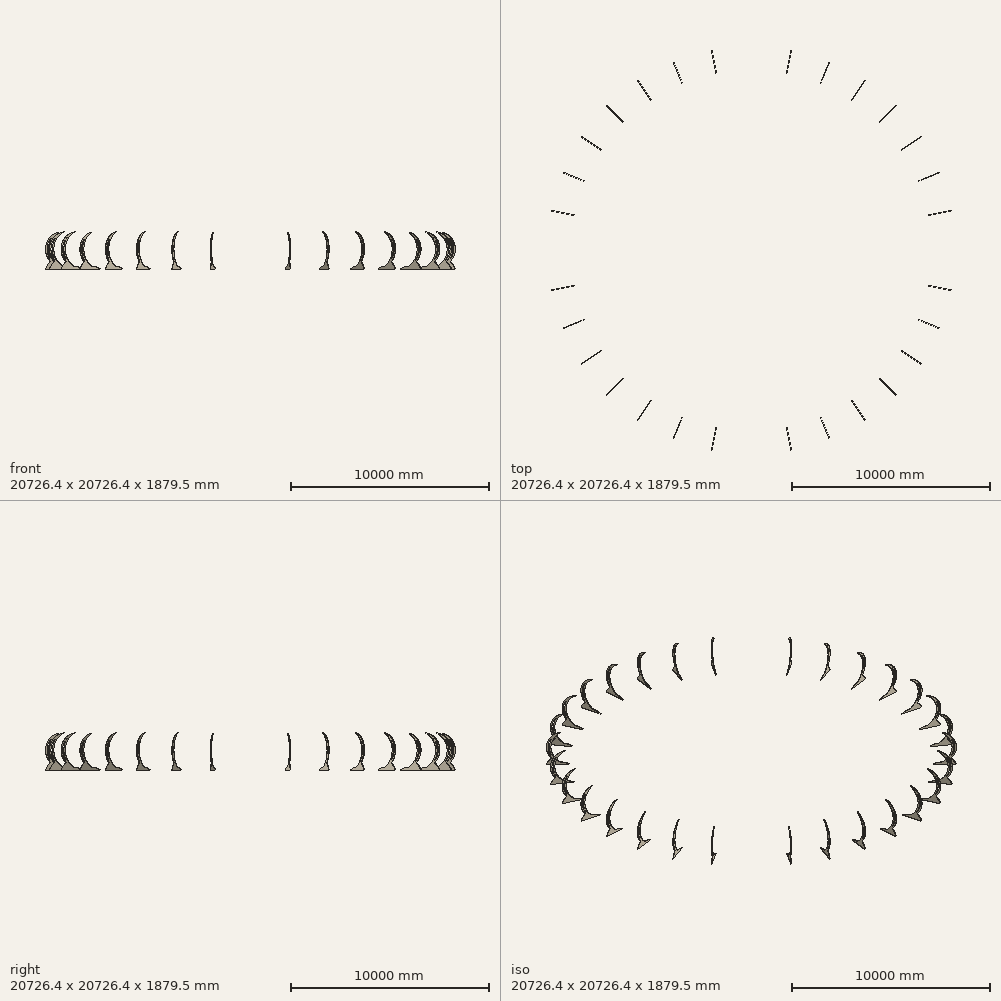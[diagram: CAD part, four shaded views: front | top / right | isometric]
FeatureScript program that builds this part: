
annotation { "Feature Type Name" : "Feature", "Feature Type Description" : "" }
export const myFeature = defineFeature(function(context is Context, id is Id, definition is map)
    precondition{}
    {
        {
            var Q0;
            Q0=qCreatedBy(makeId("Front.planeOp"),FACE);
            var sketch = newSketch(context, id + "F0", { "sketchPlane" : qUnion([Q0])});
            skLineSegment(sketch, "E0.1", {"start": v(-10363.2, 0) * mm, "end": v(-10363.2, 1219.2) * mm, "construction": true});
            skLineSegment(sketch, "E0.7", {"start": v(-9144, 0) * mm, "end": v(-10363.2, 0) * mm, "construction": true});
            skArc(sketch, "E0.8", {"start": v(-9241.93, -3.92) * mm, "mid": v(-9367.59, 73.04) * mm, "end": v(-9502.79, 131.63) * mm, "construction": true});
            skLineSegment(sketch, "E0.10", {"start": v(-9144, 0) * mm, "end": v(-9144, 1219.2) * mm, "construction": true});
            skLineSegment(sketch, "E1.top", {"start": v(-10363.2, 2438.4) * mm, "end": v(-9144, 2438.4) * mm, "construction": true});
            skLineSegment(sketch, "E1.left", {"start": v(-10363.2, 1219.2) * mm, "end": v(-10363.2, 2438.4) * mm, "construction": true});
            skLineSegment(sketch, "E1.right", {"start": v(-9144, 1219.2) * mm, "end": v(-9144, 2438.4) * mm, "construction": true});
            skLineSegment(sketch, "E2", {"start": v(-10363.2, 1219.2) * mm, "end": v(-9144, 1219.2) * mm, "construction": true});
            skLineSegment(sketch, "E3", {"start": v(-9753.6, 2438.4) * mm, "end": v(-9753.6, 0) * mm, "construction": true});
            skArc(sketch, "E4", {"start": v(-10093.04, 361.13) * mm, "mid": v(-10247.75, 195.25) * mm, "end": v(-10363.2, 0) * mm});
            skLineSegment(sketch, "E5", {"start": v(-9408.3, 60.26) * mm, "end": v(-9595.1, 1879.5) * mm, "construction": true});
            skArc(sketch, "E6", {"start": v(-9595.1, 1879.5) * mm, "mid": v(-10318.96, 1276.05) * mm, "end": v(-10093.04, 361.13) * mm});
            skArc(sketch, "E7", {"start": v(-9595.1, 1879.5) * mm, "mid": v(-10136.83, 1039.6) * mm, "end": v(-9674.58, 153.48) * mm});
            skLineSegment(sketch, "E8", {"start": v(-10363.2, 0) * mm, "end": v(-9144, 0) * mm});
            skArc(sketch, "E9.0", {"start": v(-10033.51, 1588.72) * mm, "mid": v(-10286.9, 1012.18) * mm, "end": v(-10052.1, 427.81) * mm});
            skArc(sketch, "E9.1", {"start": v(-10033.51, 1588.72) * mm, "mid": v(-10213.94, 1011) * mm, "end": v(-10052.1, 427.81) * mm});
            skPoint(sketch, "E10.center", {"position": v(-9753.6, 1219.2) * mm});
            skArc(sketch, "E11", {"start": v(-9144, 0) * mm, "mid": v(-9400.61, 106.73) * mm, "end": v(-9674.58, 153.48) * mm});
            skPoint(sketch, "E0.9.start.orphan", {"position": v(-9404.85, 135.55) * mm});
            skArc(sketch, "E12.1.0", {"start": v(-9414.16, 2077.27) * mm, "mid": v(-9259.45, 2243.15) * mm, "end": v(-9144, 2438.4) * mm, "construction": true});
            skArc(sketch, "E12.1.1", {"start": v(-9912.1, 558.9) * mm, "mid": v(-9188.24, 1162.35) * mm, "end": v(-9414.16, 2077.27) * mm, "construction": true});
            skArc(sketch, "E12.1.2", {"start": v(-9473.69, 849.68) * mm, "mid": v(-9220.3, 1426.22) * mm, "end": v(-9455.1, 2010.59) * mm, "construction": true});
            skArc(sketch, "E12.1.3", {"start": v(-9473.69, 849.68) * mm, "mid": v(-9293.26, 1427.4) * mm, "end": v(-9455.1, 2010.59) * mm, "construction": true});
            skArc(sketch, "E12.1.4", {"start": v(-9912.1, 558.9) * mm, "mid": v(-9370.37, 1398.8) * mm, "end": v(-9832.62, 2284.92) * mm, "construction": true});
            skArc(sketch, "E12.1.5", {"start": v(-10363.2, 2438.4) * mm, "mid": v(-10106.59, 2331.67) * mm, "end": v(-9832.62, 2284.92) * mm, "construction": true});
            skSolve(sketch);
        }
        {
            var Q0;
            Q0 = qSketchRegion(id + "F0", true);
            extrude(context, id + "F1", {"entities" : qUnion([Q0]), "depth" : 12.7 * mm, "hasSecondDirection" : true, "secondDirectionOppositeDirection" : true, "secondDirectionDepth" : 12.7 * mm});
        }
        {
            var Q0;
            Q0=qCreatedBy(makeId("Front.planeOp"),FACE);
            var sketch = newSketch(context, id + "F2", { "sketchPlane" : qUnion([Q0])});
            skLineSegment(sketch, "E13.bottom", {"start": v(-9144, 0) * mm, "end": v(-10363.2, 0) * mm});
            skLineSegment(sketch, "E13.top", {"start": v(-9144, 1219.2) * mm, "end": v(-10363.2, 1219.2) * mm, "construction": true});
            skLineSegment(sketch, "E13.left", {"start": v(-9144, 0) * mm, "end": v(-9144, 1219.2) * mm, "construction": true});
            skLineSegment(sketch, "E13.right", {"start": v(-10363.2, 0) * mm, "end": v(-10363.2, 1219.2) * mm, "construction": true});
            skArc(sketch, "E14", {"start": v(-9144, 0) * mm, "mid": v(-9269.66, 76.95) * mm, "end": v(-9404.85, 135.55) * mm});
            skLineSegment(sketch, "E15", {"start": v(0, 1828.8) * mm, "end": v(0, 4267.2) * mm, "construction": true});
            skLineSegment(sketch, "E16", {"start": v(-5181.6, 12008.6) * mm, "end": v(-5181.6, -5912.6) * mm, "construction": true});
            skEllipse(sketch, "E17", {"center": v(-5181.6, 3048) * mm, "majorRadius": 8960.6 * mm, "minorRadius": 5181.6 * mm, "majorAxis": v(0, 1), "construction": true});
            skPoint(sketch, "E18", {"position": v(-10363.2, 3048) * mm});
            skPoint(sketch, "E19", {"position": v(0, 3048) * mm});
            skEllipticalArc(sketch, "E20", {});
            skPoint(sketch, "E21", {"position": v(-10363.2, 663.58) * mm});
            skPoint(sketch, "E22", {"position": v(-9632.3, 1219.2) * mm});
            skArc(sketch, "E23.trimOffspring", {"start": v(-9972.96, 172) * mm, "mid": v(-10176.9, 106.03) * mm, "end": v(-10363.2, 0) * mm});
            skEllipticalArc(sketch, "E24.trimOffspring", {});
            skEllipticalArc(sketch, "E25", {});
            skFitSpline(sketch, "E26.0", {"points": [v(-10286.97, 669.24) * mm, v(-10287.02, 663.58) * mm, v(-10286.97, 657.92) * mm, v(-10286.79, 650.39) * mm, v(-10286.32, 640.99) * mm, v(-10285.4, 629.74) * mm, v(-10283.7, 614.8) * mm, v(-10280.66, 596.2) * mm, v(-10275.57, 574.03) * mm, v(-10269.05, 552.04) * mm, v(-10258.44, 522.98) * mm, v(-10241.6, 487.22) * mm, v(-10220, 452.43) * mm, v(-10199.87, 425.37) * mm, v(-10183.35, 405.5) * mm, v(-10165.42, 386.1) * mm, v(-10149.3, 370.36) * mm, v(-10135.72, 358.07) * mm, v(-10125.18, 349) * mm, v(-10116.1, 341.57) * mm, v(-10108.68, 335.7) * mm, v(-10103.02, 331.35) * mm, v(-10097.29, 327.05) * mm, v(-10089.55, 321.38) * mm, v(-10079.7, 314.43) * mm, v(-10067.62, 306.32) * mm, v(-10051.15, 295.8) * mm, v(-10029.94, 283.24) * mm, v(-10003.5, 269.12) * mm, v(-9976.16, 255.98) * mm, v(-9938.56, 239.81) * mm, v(-9889.56, 222.2) * mm, v(-9838.32, 208.25) * mm, v(-9796.23, 199.37) * mm, v(-9764.18, 193.87) * mm, v(-9731.7, 189.56) * mm, v(-9704.32, 186.98) * mm, v(-9682.28, 185.52) * mm, v(-9665.68, 184.74) * mm, v(-9651.8, 184.35) * mm, v(-9640.66, 184.19) * mm, v(-9632.3, 184.15) * mm, v(-9623.93, 184.19) * mm, v(-9612.8, 184.35) * mm, v(-9598.92, 184.74) * mm, v(-9582.31, 185.52) * mm, v(-9560.27, 186.98) * mm, v(-9532.9, 189.56) * mm, v(-9500.42, 193.87) * mm, v(-9468.36, 199.37) * mm, v(-9426.27, 208.25) * mm, v(-9375.03, 222.2) * mm, v(-9326.04, 239.81) * mm, v(-9288.44, 255.98) * mm, v(-9261.1, 269.12) * mm, v(-9234.66, 283.24) * mm, v(-9213.44, 295.8) * mm, v(-9196.98, 306.32) * mm, v(-9184.9, 314.43) * mm, v(-9175.05, 321.38) * mm, v(-9167.3, 327.05) * mm, v(-9161.57, 331.35) * mm, v(-9155.91, 335.7) * mm, v(-9148.49, 341.57) * mm, v(-9139.42, 349) * mm, v(-9128.88, 358.07) * mm, v(-9115.3, 370.36) * mm, v(-9099.18, 386.1) * mm, v(-9081.24, 405.5) * mm, v(-9064.73, 425.37) * mm, v(-9044.6, 452.43) * mm, v(-9022.99, 487.22) * mm, v(-9006.15, 522.98) * mm, v(-8995.55, 552.04) * mm, v(-8989.02, 574.03) * mm, v(-8983.94, 596.2) * mm, v(-8980.9, 614.8) * mm, v(-8979.19, 629.74) * mm, v(-8978.27, 640.99) * mm, v(-8977.8, 650.39) * mm, v(-8977.62, 657.92) * mm, v(-8977.58, 663.58) * mm, v(-8977.62, 669.24) * mm, v(-8977.8, 676.77) * mm, v(-8978.27, 686.17) * mm, v(-8979.19, 697.42) * mm, v(-8980.9, 712.37) * mm, v(-8983.94, 730.97) * mm, v(-8989.02, 753.13) * mm, v(-8995.55, 775.12) * mm, v(-9006.15, 804.18) * mm, v(-9022.99, 839.94) * mm, v(-9044.6, 874.73) * mm, v(-9064.73, 901.8) * mm, v(-9081.24, 921.67) * mm, v(-9099.18, 941.07) * mm, v(-9115.3, 956.8) * mm, v(-9128.88, 969.1) * mm, v(-9139.42, 978.16) * mm, v(-9148.49, 985.6) * mm, v(-9155.91, 991.45) * mm, v(-9161.57, 995.8) * mm, v(-9167.3, 1000.11) * mm, v(-9175.05, 1005.78) * mm, v(-9184.9, 1012.73) * mm, v(-9196.98, 1020.84) * mm, v(-9213.44, 1031.36) * mm, v(-9234.66, 1043.92) * mm, v(-9261.1, 1058.04) * mm, v(-9288.44, 1071.18) * mm, v(-9326.04, 1087.35) * mm, v(-9375.03, 1104.95) * mm, v(-9426.27, 1118.9) * mm, v(-9468.36, 1127.79) * mm, v(-9500.42, 1133.29) * mm, v(-9532.9, 1137.6) * mm, v(-9560.27, 1140.18) * mm, v(-9582.31, 1141.64) * mm, v(-9598.92, 1142.42) * mm, v(-9612.8, 1142.81) * mm, v(-9623.93, 1142.97) * mm, v(-9632.3, 1143.01) * mm, v(-9640.66, 1142.97) * mm, v(-9651.8, 1142.81) * mm, v(-9665.68, 1142.42) * mm, v(-9682.28, 1141.64) * mm, v(-9704.32, 1140.18) * mm, v(-9731.7, 1137.6) * mm, v(-9764.18, 1133.29) * mm, v(-9796.23, 1127.79) * mm, v(-9838.32, 1118.9) * mm, v(-9889.56, 1104.95) * mm, v(-9938.56, 1087.35) * mm, v(-9976.16, 1071.18) * mm, v(-10003.5, 1058.04) * mm, v(-10029.94, 1043.92) * mm, v(-10051.15, 1031.36) * mm, v(-10067.62, 1020.84) * mm, v(-10079.7, 1012.73) * mm, v(-10089.55, 1005.78) * mm, v(-10097.29, 1000.11) * mm, v(-10103.02, 995.8) * mm, v(-10108.68, 991.45) * mm, v(-10116.1, 985.6) * mm, v(-10125.18, 978.16) * mm, v(-10135.72, 969.1) * mm, v(-10149.3, 956.8) * mm, v(-10165.42, 941.07) * mm, v(-10183.35, 921.67) * mm, v(-10199.87, 901.8) * mm, v(-10220, 874.73) * mm, v(-10241.6, 839.94) * mm, v(-10258.44, 804.18) * mm, v(-10269.05, 775.12) * mm, v(-10275.57, 753.13) * mm, v(-10280.66, 730.97) * mm, v(-10283.7, 712.37) * mm, v(-10285.4, 697.42) * mm, v(-10286.32, 686.17) * mm, v(-10286.79, 676.77) * mm, v(-10286.97, 669.24) * mm, v(-10287.02, 663.58) * mm, v(-10286.97, 657.92) * mm]});
            skFitSpline(sketch, "E27.trimOffspring", {"points": [v(-8791.4, 656.31) * mm, v(-8791.35, 663.58) * mm, v(-8791.4, 670.85) * mm, v(-8791.63, 680.52) * mm, v(-8792.18, 692.59) * mm, v(-8793.28, 707.01) * mm, v(-8795.31, 726.17) * mm, v(-8798.93, 749.93) * mm, v(-8804.96, 778.12) * mm, v(-8812.64, 805.9) * mm, v(-8825.03, 842.33) * mm, v(-8844.45, 886.58) * mm, v(-8868.9, 928.78) * mm, v(-8891.3, 961.13) * mm, v(-8909.5, 984.64) * mm, v(-8929.06, 1007.35) * mm, v(-8946.46, 1025.6) * mm, v(-8961.03, 1039.74) * mm, v(-8972.27, 1050.14) * mm, v(-8981.9, 1058.6) * mm, v(-8989.76, 1065.27) * mm, v(-8995.74, 1070.2) * mm, v(-9001.78, 1075.08) * mm, v(-9009.92, 1081.48) * mm, v(-9020.24, 1089.3) * mm, v(-9032.86, 1098.4) * mm, v(-9049.98, 1110.14) * mm, v(-9071.93, 1124.1) * mm, v(-9099.09, 1139.68) * mm, v(-9127, 1154.08) * mm, v(-9165.16, 1171.7) * mm, v(-9214.5, 1190.72) * mm, v(-9265.7, 1205.69) * mm, v(-9307.56, 1215.17) * mm, v(-9339.36, 1221.03) * mm, v(-9371.52, 1225.6) * mm, v(-9398.59, 1228.36) * mm, v(-9420.37, 1229.9) * mm, v(-9436.76, 1230.73) * mm, v(-9450.47, 1231.15) * mm, v(-9461.46, 1231.31) * mm, v(-9469.71, 1231.36) * mm, v(-9477.97, 1231.31) * mm, v(-9488.95, 1231.15) * mm, v(-9502.66, 1230.73) * mm, v(-9519.06, 1229.9) * mm, v(-9540.84, 1228.36) * mm, v(-9567.9, 1225.6) * mm, v(-9600.06, 1221.03) * mm, v(-9631.87, 1215.17) * mm, v(-9673.73, 1205.69) * mm, v(-9724.92, 1190.72) * mm, v(-9774.26, 1171.7) * mm, v(-9812.42, 1154.08) * mm, v(-9840.34, 1139.68) * mm, v(-9867.5, 1124.1) * mm, v(-9889.44, 1110.14) * mm, v(-9906.57, 1098.4) * mm, v(-9919.19, 1089.3) * mm, v(-9929.5, 1081.48) * mm, v(-9937.64, 1075.08) * mm, v(-9943.69, 1070.2) * mm, v(-9949.66, 1065.27) * mm, v(-9957.52, 1058.6) * mm, v(-9967.15, 1050.14) * mm, v(-9978.4, 1039.74) * mm, v(-9992.96, 1025.6) * mm, v(-10010.37, 1007.35) * mm, v(-10029.92, 984.64) * mm, v(-10048.12, 961.13) * mm, v(-10070.53, 928.78) * mm, v(-10094.97, 886.58) * mm, v(-10114.4, 842.33) * mm, v(-10126.79, 805.9) * mm, v(-10134.46, 778.12) * mm, v(-10140.49, 749.93) * mm, v(-10144.1, 726.17) * mm, v(-10146.15, 707.01) * mm, v(-10147.24, 692.59) * mm, v(-10147.8, 680.52) * mm, v(-10148.01, 670.85) * mm, v(-10148.07, 663.58) * mm, v(-10148.01, 656.31) * mm, v(-10147.8, 646.64) * mm, v(-10147.24, 634.58) * mm, v(-10146.15, 620.15) * mm, v(-10144.1, 601) * mm, v(-10140.49, 577.23) * mm, v(-10134.46, 549.05) * mm, v(-10126.79, 521.26) * mm, v(-10114.4, 484.83) * mm, v(-10094.97, 440.58) * mm, v(-10070.53, 398.38) * mm, v(-10048.12, 366.04) * mm, v(-10029.92, 342.53) * mm, v(-10010.37, 319.81) * mm, v(-9992.96, 301.57) * mm, v(-9978.4, 287.42) * mm, v(-9967.15, 277.03) * mm, v(-9957.52, 268.56) * mm, v(-9949.66, 261.9) * mm, v(-9943.69, 256.96) * mm, v(-9937.64, 252.08) * mm, v(-9929.5, 245.69) * mm, v(-9919.19, 237.86) * mm, v(-9906.57, 228.77) * mm, v(-9889.44, 217.02) * mm, v(-9867.5, 203.07) * mm, v(-9840.34, 187.49) * mm, v(-9812.42, 173.09) * mm, v(-9774.26, 155.47) * mm, v(-9724.92, 136.44) * mm, v(-9673.73, 121.48) * mm, v(-9631.87, 112) * mm, v(-9600.06, 106.14) * mm, v(-9567.9, 101.55) * mm, v(-9540.84, 98.8) * mm, v(-9519.06, 97.26) * mm, v(-9502.66, 96.43) * mm, v(-9488.95, 96.02) * mm, v(-9477.97, 95.85) * mm, v(-9469.71, 95.8) * mm, v(-9461.46, 95.85) * mm, v(-9450.47, 96.02) * mm, v(-9436.76, 96.43) * mm, v(-9420.37, 97.26) * mm, v(-9398.59, 98.8) * mm, v(-9371.52, 101.55) * mm, v(-9339.36, 106.14) * mm, v(-9307.56, 112) * mm, v(-9265.7, 121.48) * mm, v(-9214.5, 136.44) * mm, v(-9165.16, 155.47) * mm, v(-9127, 173.09) * mm, v(-9099.09, 187.49) * mm, v(-9071.93, 203.07) * mm, v(-9049.98, 217.02) * mm, v(-9032.86, 228.77) * mm, v(-9020.24, 237.86) * mm, v(-9009.92, 245.69) * mm, v(-9001.78, 252.08) * mm, v(-8995.74, 256.96) * mm, v(-8989.76, 261.9) * mm, v(-8981.9, 268.56) * mm, v(-8972.27, 277.03) * mm, v(-8961.03, 287.42) * mm, v(-8946.46, 301.57) * mm, v(-8929.06, 319.81) * mm, v(-8909.5, 342.53) * mm, v(-8891.3, 366.04) * mm, v(-8868.9, 398.38) * mm, v(-8844.45, 440.58) * mm, v(-8825.03, 484.83) * mm, v(-8812.64, 521.26) * mm, v(-8804.96, 549.05) * mm, v(-8798.93, 577.23) * mm, v(-8795.31, 601) * mm, v(-8793.28, 620.15) * mm, v(-8792.18, 634.58) * mm, v(-8791.63, 646.64) * mm, v(-8791.4, 656.31) * mm, v(-8791.35, 663.58) * mm, v(-8791.4, 670.85) * mm]});
            skFitSpline(sketch, "E28.trimOffspring", {"points": [v(-8791.41, 656.31) * mm, v(-8791.36, 663.58) * mm, v(-8791.41, 670.85) * mm, v(-8791.63, 680.52) * mm, v(-8792.18, 692.59) * mm, v(-8793.28, 707.01) * mm, v(-8795.32, 726.16) * mm, v(-8798.94, 749.93) * mm, v(-8804.96, 778.12) * mm, v(-8812.64, 805.9) * mm, v(-8825.03, 842.33) * mm, v(-8844.46, 886.58) * mm, v(-8868.9, 928.78) * mm, v(-8891.3, 961.13) * mm, v(-8909.5, 984.63) * mm, v(-8929.06, 1007.35) * mm, v(-8946.46, 1025.59) * mm, v(-8961.03, 1039.74) * mm, v(-8972.27, 1050.13) * mm, v(-8981.9, 1058.6) * mm, v(-8989.76, 1065.27) * mm, v(-8995.74, 1070.2) * mm, v(-9001.78, 1075.08) * mm, v(-9009.92, 1081.48) * mm, v(-9020.24, 1089.3) * mm, v(-9032.86, 1098.4) * mm, v(-9049.98, 1110.14) * mm, v(-9071.93, 1124.1) * mm, v(-9099.09, 1139.67) * mm, v(-9127, 1154.07) * mm, v(-9165.16, 1171.69) * mm, v(-9214.5, 1190.72) * mm, v(-9265.7, 1205.68) * mm, v(-9307.56, 1215.17) * mm, v(-9339.36, 1221.02) * mm, v(-9371.52, 1225.6) * mm, v(-9398.59, 1228.35) * mm, v(-9420.37, 1229.9) * mm, v(-9436.76, 1230.73) * mm, v(-9450.47, 1231.14) * mm, v(-9461.46, 1231.31) * mm, v(-9469.71, 1231.35) * mm, v(-9477.97, 1231.31) * mm, v(-9488.96, 1231.14) * mm, v(-9502.66, 1230.73) * mm, v(-9519.06, 1229.9) * mm, v(-9540.84, 1228.35) * mm, v(-9567.9, 1225.6) * mm, v(-9600.06, 1221.02) * mm, v(-9631.87, 1215.17) * mm, v(-9673.73, 1205.68) * mm, v(-9724.92, 1190.72) * mm, v(-9774.26, 1171.69) * mm, v(-9812.42, 1154.07) * mm, v(-9840.34, 1139.67) * mm, v(-9867.5, 1124.1) * mm, v(-9889.44, 1110.14) * mm, v(-9906.57, 1098.4) * mm, v(-9919.19, 1089.3) * mm, v(-9929.5, 1081.48) * mm, v(-9937.64, 1075.08) * mm, v(-9943.69, 1070.2) * mm, v(-9949.66, 1065.27) * mm, v(-9957.52, 1058.6) * mm, v(-9967.15, 1050.13) * mm, v(-9978.4, 1039.74) * mm, v(-9992.96, 1025.59) * mm, v(-10010.37, 1007.35) * mm, v(-10029.92, 984.63) * mm, v(-10048.12, 961.13) * mm, v(-10070.53, 928.78) * mm, v(-10094.97, 886.58) * mm, v(-10114.4, 842.33) * mm, v(-10126.78, 805.9) * mm, v(-10134.46, 778.12) * mm, v(-10140.49, 749.93) * mm, v(-10144.1, 726.16) * mm, v(-10146.15, 707.01) * mm, v(-10147.24, 692.59) * mm, v(-10147.8, 680.52) * mm, v(-10148.01, 670.85) * mm, v(-10148.07, 663.58) * mm, v(-10148.01, 656.31) * mm, v(-10147.8, 646.64) * mm, v(-10147.24, 634.57) * mm, v(-10146.15, 620.15) * mm, v(-10144.1, 601) * mm, v(-10140.49, 577.23) * mm, v(-10134.46, 549.04) * mm, v(-10126.78, 521.26) * mm, v(-10114.4, 484.83) * mm, v(-10094.97, 440.58) * mm, v(-10070.53, 398.38) * mm, v(-10048.12, 366.03) * mm, v(-10029.92, 342.53) * mm, v(-10010.37, 319.8) * mm, v(-9992.96, 301.57) * mm, v(-9978.4, 287.42) * mm, v(-9967.15, 277.03) * mm, v(-9957.52, 268.55) * mm, v(-9949.66, 261.9) * mm, v(-9943.69, 256.96) * mm, v(-9937.64, 252.08) * mm, v(-9929.5, 245.68) * mm, v(-9919.19, 237.86) * mm, v(-9906.57, 228.77) * mm, v(-9889.44, 217.02) * mm, v(-9867.5, 203.06) * mm, v(-9840.34, 187.49) * mm, v(-9812.42, 173.09) * mm, v(-9774.26, 155.47) * mm, v(-9724.92, 136.44) * mm, v(-9673.73, 121.48) * mm, v(-9631.87, 112) * mm, v(-9600.06, 106.14) * mm, v(-9567.9, 101.55) * mm, v(-9540.84, 98.8) * mm, v(-9519.06, 97.26) * mm, v(-9502.66, 96.43) * mm, v(-9488.96, 96.02) * mm, v(-9477.97, 95.85) * mm, v(-9469.71, 95.8) * mm, v(-9461.46, 95.85) * mm, v(-9450.47, 96.02) * mm, v(-9436.76, 96.43) * mm, v(-9420.37, 97.26) * mm, v(-9398.59, 98.8) * mm, v(-9371.52, 101.55) * mm, v(-9339.36, 106.14) * mm, v(-9307.56, 112) * mm, v(-9265.7, 121.48) * mm, v(-9214.5, 136.44) * mm, v(-9165.16, 155.47) * mm, v(-9127, 173.09) * mm, v(-9099.09, 187.49) * mm, v(-9071.93, 203.06) * mm, v(-9049.98, 217.02) * mm, v(-9032.86, 228.77) * mm, v(-9020.24, 237.86) * mm, v(-9009.92, 245.68) * mm, v(-9001.78, 252.08) * mm, v(-8995.74, 256.96) * mm, v(-8989.76, 261.9) * mm, v(-8981.9, 268.55) * mm, v(-8972.27, 277.03) * mm, v(-8961.03, 287.42) * mm, v(-8946.46, 301.57) * mm, v(-8929.06, 319.8) * mm, v(-8909.5, 342.53) * mm, v(-8891.3, 366.03) * mm, v(-8868.9, 398.38) * mm, v(-8844.46, 440.58) * mm, v(-8825.03, 484.83) * mm, v(-8812.64, 521.26) * mm, v(-8804.96, 549.04) * mm, v(-8798.94, 577.23) * mm, v(-8795.32, 601) * mm, v(-8793.28, 620.15) * mm, v(-8792.18, 634.57) * mm, v(-8791.63, 646.64) * mm, v(-8791.41, 656.31) * mm, v(-8791.36, 663.58) * mm, v(-8791.41, 670.85) * mm]});
            skArc(sketch, "E29", {"start": v(-12031.57, 534.37) * mm, "mid": v(-12125.4, 109.1) * mm, "end": v(-12031.57, -316.19) * mm, "construction": true});
            skLineSegment(sketch, "E30.bottom", {"start": v(-12031.57, 534.37) * mm, "end": v(-12031.57, -316.19) * mm, "construction": true});
            const initialGuessF2  = {"E20": [-9.632296562194824, 0.6635811924934387, -1, 0, 0.7309034378051766, 0.5556188075065615, 3.9807734677145237, 1.0859331361887579], "E24.trimOffspring": [-9.632296562194824, 0.6635811924934387, -1, 0, 0.7309034378051766, 0.5556188075065615, 1.88723070716401, 2.302411839465053], "E25": [-9.469712257385254, 0.6635811924934387, 1, 0, 0.6021368416979103, 0.49155730598015346, 0.9992570800552321, 5.283928227124344]};
            skSetInitialGuess(sketch, initialGuessF2);
            skSolve(sketch);
        }
        {
            var Q0;
            Q0=makeQuery(id+"F1.opExtrude","SWEPT_FACE",FACE,{"disambiguationData":[OSD([sQuery(id+"F0.wireOp",EDGE,"E8")])]});
            var sketch = newSketch(context, id + "F3", { "sketchPlane" : qUnion([Q0])});
            skLineSegment(sketch, "E31", {"start": v(-10049.02, 12.7) * mm, "end": v(-10049.02, -38.1) * mm});
            skLineSegment(sketch, "E32", {"start": v(-9379.36, 12.7) * mm, "end": v(-9379.36, -38.1) * mm});
            skSolve(sketch);
        }
        {
            var Q0;
            Q0=sQuery(id+"F3.wireOp",EDGE,"E32");
            cPlane(context, id + "F4", {"entities" : qUnion([Q0]), "cplaneType" : CPlaneType.LINE_ANGLE, "offset" : 152.4 * mm, "angle" : 30 * degree, "width" : 152.4 * mm, "height" : 152.4 * mm});
        }
        {
            var Q0;
            Q0=sQuery(id+"F3.wireOp",EDGE,"E31");
            cPlane(context, id + "F5", {"entities" : qUnion([Q0]), "cplaneType" : CPlaneType.LINE_ANGLE, "offset" : 152.4 * mm, "angle" : 150 * degree, "width" : 152.4 * mm, "height" : 152.4 * mm});
        }
        {
            var Q0;
            Q0=qCreatedBy(id+"F4.planeOp",FACE);
            var sketch = newSketch(context, id + "F6", { "sketchPlane" : qUnion([Q0])});
            skLineSegment(sketch, "E33", {"start": v(-8122.77, -393.54) * mm, "end": v(-8122.77, 418.94) * mm});
            skLineSegment(sketch, "E34.0.0", {"start": v(-13115.2, 1419.4) * mm, "end": v(-11896, 1419.4) * mm, "construction": true});
            skLineSegment(sketch, "E35.2", {"start": v(-11896, 1419.4) * mm, "end": v(-11896, 2638.6) * mm, "construction": true});
            skLineSegment(sketch, "E35.1", {"start": v(-11896, 2638.6) * mm, "end": v(-13115.2, 2638.6) * mm, "construction": true});
            skLineSegment(sketch, "E35.0", {"start": v(-13115.2, 1419.4) * mm, "end": v(-13115.2, 2638.6) * mm, "construction": true});
            skFitSpline(sketch, "E36.0", {"points": [v(-13121.5, 2089.98) * mm, v(-13121.57, 2082.97) * mm, v(-13121.5, 2075.96) * mm, v(-13121.28, 2066.63) * mm, v(-13120.71, 2055) * mm, v(-13119.58, 2041.08) * mm, v(-13117.46, 2022.6) * mm, v(-13113.71, 1999.65) * mm, v(-13107.45, 1972.4) * mm, v(-13099.47, 1945.48) * mm, v(-13086.55, 1910.1) * mm, v(-13066.22, 1866.96) * mm, v(-13040.48, 1825.56) * mm, v(-13016.76, 1793.67) * mm, v(-12997.42, 1770.4) * mm, v(-12976.57, 1747.86) * mm, v(-12957.96, 1729.69) * mm, v(-12942.34, 1715.55) * mm, v(-12930.26, 1705.16) * mm, v(-12919.9, 1696.67) * mm, v(-12911.42, 1689.98) * mm, v(-12904.98, 1685.02) * mm, v(-12898.45, 1680.13) * mm, v(-12889.67, 1673.69) * mm, v(-12878.5, 1665.81) * mm, v(-12864.84, 1656.64) * mm, v(-12846.27, 1644.78) * mm, v(-12822.41, 1630.66) * mm, v(-12792.82, 1614.85) * mm, v(-12762.33, 1600.2) * mm, v(-12720.54, 1582.24) * mm, v(-12666.35, 1562.77) * mm, v(-12609.94, 1547.4) * mm, v(-12563.72, 1537.66) * mm, v(-12528.58, 1531.63) * mm, v(-12493, 1526.91) * mm, v(-12463.05, 1524.08) * mm, v(-12438.94, 1522.49) * mm, v(-12420.79, 1521.63) * mm, v(-12405.6, 1521.2) * mm, v(-12393.44, 1521.03) * mm, v(-12384.3, 1520.99) * mm, v(-12375.15, 1521.03) * mm, v(-12362.98, 1521.2) * mm, v(-12347.8, 1521.63) * mm, v(-12329.65, 1522.49) * mm, v(-12305.54, 1524.08) * mm, v(-12275.59, 1526.91) * mm, v(-12240.01, 1531.63) * mm, v(-12204.87, 1537.66) * mm, v(-12158.65, 1547.4) * mm, v(-12102.24, 1562.77) * mm, v(-12048.05, 1582.24) * mm, v(-12006.26, 1600.2) * mm, v(-11975.77, 1614.85) * mm, v(-11946.18, 1630.66) * mm, v(-11922.32, 1644.78) * mm, v(-11903.75, 1656.64) * mm, v(-11890.08, 1665.81) * mm, v(-11878.92, 1673.69) * mm, v(-11870.13, 1680.13) * mm, v(-11863.61, 1685.02) * mm, v(-11857.17, 1689.98) * mm, v(-11848.7, 1696.67) * mm, v(-11838.33, 1705.16) * mm, v(-11826.25, 1715.55) * mm, v(-11810.63, 1729.69) * mm, v(-11792.02, 1747.86) * mm, v(-11771.17, 1770.4) * mm, v(-11751.83, 1793.67) * mm, v(-11728.1, 1825.56) * mm, v(-11702.37, 1866.96) * mm, v(-11682.04, 1910.1) * mm, v(-11669.12, 1945.48) * mm, v(-11661.14, 1972.4) * mm, v(-11654.88, 1999.65) * mm, v(-11651.12, 2022.6) * mm, v(-11649.01, 2041.08) * mm, v(-11647.88, 2055) * mm, v(-11647.3, 2066.63) * mm, v(-11647.08, 2075.96) * mm, v(-11647.02, 2082.97) * mm, v(-11647.08, 2089.98) * mm, v(-11647.3, 2099.3) * mm, v(-11647.88, 2110.94) * mm, v(-11649.01, 2124.86) * mm, v(-11651.12, 2143.34) * mm, v(-11654.88, 2166.3) * mm, v(-11661.14, 2193.54) * mm, v(-11669.12, 2220.46) * mm, v(-11682.04, 2255.84) * mm, v(-11702.37, 2298.98) * mm, v(-11728.1, 2340.39) * mm, v(-11751.83, 2372.28) * mm, v(-11771.17, 2395.53) * mm, v(-11792.02, 2418.09) * mm, v(-11810.63, 2436.25) * mm, v(-11826.25, 2450.4) * mm, v(-11838.33, 2460.79) * mm, v(-11848.7, 2469.28) * mm, v(-11857.17, 2475.96) * mm, v(-11863.61, 2480.92) * mm, v(-11870.13, 2485.82) * mm, v(-11878.92, 2492.25) * mm, v(-11890.08, 2500.13) * mm, v(-11903.75, 2509.3) * mm, v(-11922.32, 2521.16) * mm, v(-11946.18, 2535.29) * mm, v(-11975.77, 2551.1) * mm, v(-12006.26, 2565.74) * mm, v(-12048.05, 2583.7) * mm, v(-12102.24, 2603.17) * mm, v(-12158.65, 2618.53) * mm, v(-12204.87, 2628.28) * mm, v(-12240.01, 2634.31) * mm, v(-12275.59, 2639.03) * mm, v(-12305.54, 2641.86) * mm, v(-12329.65, 2643.45) * mm, v(-12347.8, 2644.3) * mm, v(-12362.98, 2644.74) * mm, v(-12375.15, 2644.91) * mm, v(-12384.3, 2644.95) * mm, v(-12393.44, 2644.91) * mm, v(-12405.6, 2644.74) * mm, v(-12420.79, 2644.3) * mm, v(-12438.94, 2643.45) * mm, v(-12463.05, 2641.86) * mm, v(-12493, 2639.03) * mm, v(-12528.58, 2634.31) * mm, v(-12563.72, 2628.28) * mm, v(-12609.94, 2618.53) * mm, v(-12666.35, 2603.17) * mm, v(-12720.54, 2583.7) * mm, v(-12762.33, 2565.74) * mm, v(-12792.82, 2551.1) * mm, v(-12822.41, 2535.29) * mm, v(-12846.27, 2521.16) * mm, v(-12864.84, 2509.3) * mm, v(-12878.5, 2500.13) * mm, v(-12889.67, 2492.25) * mm, v(-12898.45, 2485.82) * mm, v(-12904.98, 2480.92) * mm, v(-12911.42, 2475.96) * mm, v(-12919.9, 2469.28) * mm, v(-12930.26, 2460.79) * mm, v(-12942.34, 2450.4) * mm, v(-12957.96, 2436.25) * mm, v(-12976.57, 2418.09) * mm, v(-12997.42, 2395.53) * mm, v(-13016.76, 2372.28) * mm, v(-13040.48, 2340.39) * mm, v(-13066.22, 2298.98) * mm, v(-13086.55, 2255.84) * mm, v(-13099.47, 2220.46) * mm, v(-13107.45, 2193.54) * mm, v(-13113.71, 2166.3) * mm, v(-13117.46, 2143.34) * mm, v(-13119.58, 2124.86) * mm, v(-13120.71, 2110.94) * mm, v(-13121.28, 2099.3) * mm, v(-13121.5, 2089.98) * mm, v(-13121.57, 2082.97) * mm, v(-13121.5, 2075.96) * mm], "construction": true});
            skFitSpline(sketch, "E37.0", {"points": [v(-11625.95, 2076.96) * mm, v(-11625.9, 2082.97) * mm, v(-11625.95, 2088.98) * mm, v(-11626.14, 2096.99) * mm, v(-11626.6, 2106.97) * mm, v(-11627.5, 2118.9) * mm, v(-11629.19, 2134.76) * mm, v(-11632.18, 2154.46) * mm, v(-11637.19, 2177.85) * mm, v(-11643.58, 2200.97) * mm, v(-11653.91, 2231.38) * mm, v(-11670.2, 2268.5) * mm, v(-11690.85, 2304.17) * mm, v(-11709.9, 2331.69) * mm, v(-11725.45, 2351.77) * mm, v(-11742.23, 2371.26) * mm, v(-11757.22, 2386.97) * mm, v(-11769.81, 2399.2) * mm, v(-11779.55, 2408.2) * mm, v(-11787.9, 2415.56) * mm, v(-11794.74, 2421.35) * mm, v(-11799.94, 2425.64) * mm, v(-11805.2, 2429.89) * mm, v(-11812.3, 2435.47) * mm, v(-11821.3, 2442.3) * mm, v(-11832.34, 2450.25) * mm, v(-11847.35, 2460.54) * mm, v(-11866.63, 2472.8) * mm, v(-11890.56, 2486.53) * mm, v(-11915.23, 2499.26) * mm, v(-11949.05, 2514.87) * mm, v(-11992.95, 2531.8) * mm, v(-12038.67, 2545.18) * mm, v(-12076.15, 2553.67) * mm, v(-12104.66, 2558.92) * mm, v(-12133.51, 2563.03) * mm, v(-12157.8, 2565.5) * mm, v(-12177.37, 2566.88) * mm, v(-12192.1, 2567.63) * mm, v(-12204.42, 2568) * mm, v(-12214.3, 2568.15) * mm, v(-12221.7, 2568.2) * mm, v(-12229.13, 2568.15) * mm, v(-12239, 2568) * mm, v(-12251.32, 2567.63) * mm, v(-12266.05, 2566.88) * mm, v(-12285.61, 2565.5) * mm, v(-12309.9, 2563.03) * mm, v(-12338.76, 2558.92) * mm, v(-12367.27, 2553.67) * mm, v(-12404.75, 2545.18) * mm, v(-12450.47, 2531.8) * mm, v(-12494.37, 2514.87) * mm, v(-12528.2, 2499.26) * mm, v(-12552.86, 2486.53) * mm, v(-12576.8, 2472.8) * mm, v(-12596.07, 2460.54) * mm, v(-12611.08, 2450.25) * mm, v(-12622.11, 2442.3) * mm, v(-12631.12, 2435.47) * mm, v(-12638.22, 2429.89) * mm, v(-12643.48, 2425.64) * mm, v(-12648.68, 2421.35) * mm, v(-12655.51, 2415.56) * mm, v(-12663.87, 2408.2) * mm, v(-12673.6, 2399.2) * mm, v(-12686.2, 2386.97) * mm, v(-12701.19, 2371.26) * mm, v(-12717.97, 2351.77) * mm, v(-12733.51, 2331.69) * mm, v(-12752.57, 2304.17) * mm, v(-12773.22, 2268.5) * mm, v(-12789.5, 2231.38) * mm, v(-12799.84, 2200.97) * mm, v(-12806.23, 2177.85) * mm, v(-12811.23, 2154.46) * mm, v(-12814.23, 2134.76) * mm, v(-12815.92, 2118.9) * mm, v(-12816.83, 2106.97) * mm, v(-12817.28, 2096.99) * mm, v(-12817.47, 2088.98) * mm, v(-12817.51, 2082.97) * mm, v(-12817.47, 2076.96) * mm, v(-12817.28, 2068.96) * mm, v(-12816.83, 2058.98) * mm, v(-12815.92, 2047.04) * mm, v(-12814.23, 2031.18) * mm, v(-12811.23, 2011.49) * mm, v(-12806.23, 1988.1) * mm, v(-12799.84, 1964.97) * mm, v(-12789.5, 1934.57) * mm, v(-12773.22, 1897.45) * mm, v(-12752.57, 1861.77) * mm, v(-12733.51, 1834.26) * mm, v(-12717.97, 1814.17) * mm, v(-12701.19, 1794.68) * mm, v(-12686.2, 1778.97) * mm, v(-12673.6, 1766.74) * mm, v(-12663.87, 1757.74) * mm, v(-12655.51, 1750.39) * mm, v(-12648.68, 1744.6) * mm, v(-12643.48, 1740.3) * mm, v(-12638.22, 1736.05) * mm, v(-12631.12, 1730.48) * mm, v(-12622.11, 1723.65) * mm, v(-12611.08, 1715.7) * mm, v(-12596.07, 1705.4) * mm, v(-12576.8, 1693.14) * mm, v(-12552.86, 1679.41) * mm, v(-12528.2, 1666.69) * mm, v(-12494.37, 1651.07) * mm, v(-12450.47, 1634.14) * mm, v(-12404.75, 1620.77) * mm, v(-12367.27, 1612.27) * mm, v(-12338.76, 1607.03) * mm, v(-12309.9, 1602.91) * mm, v(-12285.61, 1600.45) * mm, v(-12266.05, 1599.06) * mm, v(-12251.32, 1598.31) * mm, v(-12239, 1597.94) * mm, v(-12229.13, 1597.79) * mm, v(-12221.7, 1597.75) * mm, v(-12214.3, 1597.79) * mm, v(-12204.42, 1597.94) * mm, v(-12192.1, 1598.31) * mm, v(-12177.37, 1599.06) * mm, v(-12157.8, 1600.45) * mm, v(-12133.51, 1602.91) * mm, v(-12104.66, 1607.03) * mm, v(-12076.15, 1612.27) * mm, v(-12038.67, 1620.77) * mm, v(-11992.95, 1634.14) * mm, v(-11949.05, 1651.07) * mm, v(-11915.23, 1666.69) * mm, v(-11890.56, 1679.41) * mm, v(-11866.63, 1693.14) * mm, v(-11847.35, 1705.4) * mm, v(-11832.34, 1715.7) * mm, v(-11821.3, 1723.65) * mm, v(-11812.3, 1730.48) * mm, v(-11805.2, 1736.05) * mm, v(-11799.94, 1740.3) * mm, v(-11794.74, 1744.6) * mm, v(-11787.9, 1750.39) * mm, v(-11779.55, 1757.74) * mm, v(-11769.81, 1766.74) * mm, v(-11757.22, 1778.97) * mm, v(-11742.23, 1794.68) * mm, v(-11725.45, 1814.17) * mm, v(-11709.9, 1834.26) * mm, v(-11690.85, 1861.77) * mm, v(-11670.2, 1897.45) * mm, v(-11653.91, 1934.57) * mm, v(-11643.58, 1964.97) * mm, v(-11637.19, 1988.1) * mm, v(-11632.18, 2011.49) * mm, v(-11629.19, 2031.18) * mm, v(-11627.5, 2047.04) * mm, v(-11626.6, 2058.98) * mm, v(-11626.14, 2068.96) * mm, v(-11625.95, 2076.96) * mm, v(-11625.9, 2082.97) * mm, v(-11625.95, 2088.98) * mm], "construction": true});
            skFitSpline(sketch, "E38.0", {"points": [v(-13121.5, 2089.98) * mm, v(-13121.57, 2082.97) * mm, v(-13121.5, 2075.96) * mm, v(-13121.28, 2066.63) * mm, v(-13120.71, 2055) * mm, v(-13119.58, 2041.08) * mm, v(-13117.46, 2022.6) * mm, v(-13113.71, 1999.65) * mm, v(-13107.45, 1972.4) * mm, v(-13099.47, 1945.48) * mm, v(-13086.55, 1910.1) * mm, v(-13066.22, 1866.96) * mm, v(-13040.48, 1825.56) * mm, v(-13016.76, 1793.67) * mm, v(-12997.42, 1770.4) * mm, v(-12976.57, 1747.86) * mm, v(-12957.96, 1729.69) * mm, v(-12942.34, 1715.55) * mm, v(-12930.26, 1705.16) * mm, v(-12919.9, 1696.67) * mm, v(-12911.42, 1689.98) * mm, v(-12904.98, 1685.02) * mm, v(-12898.45, 1680.13) * mm, v(-12889.67, 1673.69) * mm, v(-12878.5, 1665.81) * mm, v(-12864.84, 1656.64) * mm, v(-12846.27, 1644.78) * mm, v(-12822.41, 1630.66) * mm, v(-12792.82, 1614.85) * mm, v(-12762.33, 1600.2) * mm, v(-12720.54, 1582.24) * mm, v(-12666.35, 1562.77) * mm, v(-12609.94, 1547.4) * mm, v(-12563.72, 1537.66) * mm, v(-12528.58, 1531.63) * mm, v(-12493, 1526.91) * mm, v(-12463.05, 1524.08) * mm, v(-12438.94, 1522.49) * mm, v(-12420.79, 1521.63) * mm, v(-12405.6, 1521.2) * mm, v(-12393.44, 1521.03) * mm, v(-12384.3, 1520.99) * mm, v(-12375.15, 1521.03) * mm, v(-12362.98, 1521.2) * mm, v(-12347.8, 1521.63) * mm, v(-12329.65, 1522.49) * mm, v(-12305.54, 1524.08) * mm, v(-12275.59, 1526.91) * mm, v(-12240.01, 1531.63) * mm, v(-12204.87, 1537.66) * mm, v(-12158.65, 1547.4) * mm, v(-12102.24, 1562.77) * mm, v(-12048.05, 1582.24) * mm, v(-12006.26, 1600.2) * mm, v(-11975.77, 1614.85) * mm, v(-11946.18, 1630.66) * mm, v(-11922.32, 1644.78) * mm, v(-11903.75, 1656.64) * mm, v(-11890.08, 1665.81) * mm, v(-11878.92, 1673.69) * mm, v(-11870.13, 1680.13) * mm, v(-11863.61, 1685.02) * mm, v(-11857.17, 1689.98) * mm, v(-11848.7, 1696.67) * mm, v(-11838.33, 1705.16) * mm, v(-11826.25, 1715.55) * mm, v(-11810.63, 1729.69) * mm, v(-11792.02, 1747.86) * mm, v(-11771.17, 1770.4) * mm, v(-11751.83, 1793.67) * mm, v(-11728.1, 1825.56) * mm, v(-11702.37, 1866.96) * mm, v(-11682.04, 1910.1) * mm, v(-11669.12, 1945.48) * mm, v(-11661.14, 1972.4) * mm, v(-11654.88, 1999.65) * mm, v(-11651.12, 2022.6) * mm, v(-11649.01, 2041.08) * mm, v(-11647.88, 2055) * mm, v(-11647.3, 2066.63) * mm, v(-11647.08, 2075.96) * mm, v(-11647.02, 2082.97) * mm, v(-11647.08, 2089.98) * mm, v(-11647.3, 2099.3) * mm, v(-11647.88, 2110.94) * mm, v(-11649.01, 2124.86) * mm, v(-11651.12, 2143.34) * mm, v(-11654.88, 2166.3) * mm, v(-11661.14, 2193.54) * mm, v(-11669.12, 2220.46) * mm, v(-11682.04, 2255.84) * mm, v(-11702.37, 2298.98) * mm, v(-11728.1, 2340.39) * mm, v(-11751.83, 2372.28) * mm, v(-11771.17, 2395.53) * mm, v(-11792.02, 2418.09) * mm, v(-11810.63, 2436.25) * mm, v(-11826.25, 2450.4) * mm, v(-11838.33, 2460.79) * mm, v(-11848.7, 2469.28) * mm, v(-11857.17, 2475.96) * mm, v(-11863.61, 2480.92) * mm, v(-11870.13, 2485.82) * mm, v(-11878.92, 2492.25) * mm, v(-11890.08, 2500.13) * mm, v(-11903.75, 2509.3) * mm, v(-11922.32, 2521.16) * mm, v(-11946.18, 2535.29) * mm, v(-11975.77, 2551.1) * mm, v(-12006.26, 2565.74) * mm, v(-12048.05, 2583.7) * mm, v(-12102.24, 2603.17) * mm, v(-12158.65, 2618.53) * mm, v(-12204.87, 2628.28) * mm, v(-12240.01, 2634.31) * mm, v(-12275.59, 2639.03) * mm, v(-12305.54, 2641.86) * mm, v(-12329.65, 2643.45) * mm, v(-12347.8, 2644.3) * mm, v(-12362.98, 2644.74) * mm, v(-12375.15, 2644.91) * mm, v(-12384.3, 2644.95) * mm, v(-12393.44, 2644.91) * mm, v(-12405.6, 2644.74) * mm, v(-12420.79, 2644.3) * mm, v(-12438.94, 2643.45) * mm, v(-12463.05, 2641.86) * mm, v(-12493, 2639.03) * mm, v(-12528.58, 2634.31) * mm, v(-12563.72, 2628.28) * mm, v(-12609.94, 2618.53) * mm, v(-12666.35, 2603.17) * mm, v(-12720.54, 2583.7) * mm, v(-12762.33, 2565.74) * mm, v(-12792.82, 2551.1) * mm, v(-12822.41, 2535.29) * mm, v(-12846.27, 2521.16) * mm, v(-12864.84, 2509.3) * mm, v(-12878.5, 2500.13) * mm, v(-12889.67, 2492.25) * mm, v(-12898.45, 2485.82) * mm, v(-12904.98, 2480.92) * mm, v(-12911.42, 2475.96) * mm, v(-12919.9, 2469.28) * mm, v(-12930.26, 2460.79) * mm, v(-12942.34, 2450.4) * mm, v(-12957.96, 2436.25) * mm, v(-12976.57, 2418.09) * mm, v(-12997.42, 2395.53) * mm, v(-13016.76, 2372.28) * mm, v(-13040.48, 2340.39) * mm, v(-13066.22, 2298.98) * mm, v(-13086.55, 2255.84) * mm, v(-13099.47, 2220.46) * mm, v(-13107.45, 2193.54) * mm, v(-13113.71, 2166.3) * mm, v(-13117.46, 2143.34) * mm, v(-13119.58, 2124.86) * mm, v(-13120.71, 2110.94) * mm, v(-13121.28, 2099.3) * mm, v(-13121.5, 2089.98) * mm, v(-13121.57, 2082.97) * mm, v(-13121.5, 2075.96) * mm], "construction": true});
            skArc(sketch, "E39.0", {"start": v(-11896, 1427.18) * mm, "mid": v(-12011.67, 1498.28) * mm, "end": v(-12135.52, 1553.94) * mm, "construction": true});
            skArc(sketch, "E40.0", {"start": v(-12745.92, 1593.21) * mm, "mid": v(-12938.6, 1528.06) * mm, "end": v(-13115.2, 1427.18) * mm, "construction": true});
            skFitSpline(sketch, "E41.trimOffspring", {"points": [v(-13121.5, 2089.98) * mm, v(-13121.57, 2082.97) * mm, v(-13121.5, 2075.96) * mm, v(-13121.28, 2066.63) * mm, v(-13120.71, 2055) * mm, v(-13119.58, 2041.08) * mm, v(-13117.46, 2022.6) * mm, v(-13113.71, 1999.65) * mm, v(-13107.45, 1972.4) * mm, v(-13099.47, 1945.48) * mm, v(-13086.55, 1910.1) * mm, v(-13066.22, 1866.96) * mm, v(-13040.48, 1825.56) * mm, v(-13016.76, 1793.67) * mm, v(-12997.42, 1770.4) * mm, v(-12976.57, 1747.86) * mm, v(-12957.96, 1729.69) * mm, v(-12942.34, 1715.55) * mm, v(-12930.26, 1705.16) * mm, v(-12919.9, 1696.67) * mm, v(-12911.42, 1689.98) * mm, v(-12904.98, 1685.02) * mm, v(-12898.45, 1680.13) * mm, v(-12889.67, 1673.69) * mm, v(-12878.5, 1665.81) * mm, v(-12864.84, 1656.64) * mm, v(-12846.27, 1644.78) * mm, v(-12822.41, 1630.66) * mm, v(-12792.82, 1614.85) * mm, v(-12762.33, 1600.2) * mm, v(-12720.54, 1582.24) * mm, v(-12666.35, 1562.77) * mm, v(-12609.94, 1547.4) * mm, v(-12563.72, 1537.66) * mm, v(-12528.58, 1531.63) * mm, v(-12493, 1526.91) * mm, v(-12463.05, 1524.08) * mm, v(-12438.94, 1522.49) * mm, v(-12420.79, 1521.63) * mm, v(-12405.6, 1521.2) * mm, v(-12393.44, 1521.03) * mm, v(-12384.3, 1520.99) * mm, v(-12375.15, 1521.03) * mm, v(-12362.98, 1521.2) * mm, v(-12347.8, 1521.63) * mm, v(-12329.65, 1522.49) * mm, v(-12305.54, 1524.08) * mm, v(-12275.59, 1526.91) * mm, v(-12240.01, 1531.63) * mm, v(-12204.87, 1537.66) * mm, v(-12158.65, 1547.4) * mm, v(-12102.24, 1562.77) * mm, v(-12048.05, 1582.24) * mm, v(-12006.26, 1600.2) * mm, v(-11975.77, 1614.85) * mm, v(-11946.18, 1630.66) * mm, v(-11922.32, 1644.78) * mm, v(-11903.75, 1656.64) * mm, v(-11890.08, 1665.81) * mm, v(-11878.92, 1673.69) * mm, v(-11870.13, 1680.13) * mm, v(-11863.61, 1685.02) * mm, v(-11857.17, 1689.98) * mm, v(-11848.7, 1696.67) * mm, v(-11838.33, 1705.16) * mm, v(-11826.25, 1715.55) * mm, v(-11810.63, 1729.69) * mm, v(-11792.02, 1747.86) * mm, v(-11771.17, 1770.4) * mm, v(-11751.83, 1793.67) * mm, v(-11728.1, 1825.56) * mm, v(-11702.37, 1866.96) * mm, v(-11682.04, 1910.1) * mm, v(-11669.12, 1945.48) * mm, v(-11661.14, 1972.4) * mm, v(-11654.88, 1999.65) * mm, v(-11651.12, 2022.6) * mm, v(-11649.01, 2041.08) * mm, v(-11647.88, 2055) * mm, v(-11647.3, 2066.63) * mm, v(-11647.08, 2075.96) * mm, v(-11647.02, 2082.97) * mm, v(-11647.08, 2089.98) * mm, v(-11647.3, 2099.3) * mm, v(-11647.88, 2110.94) * mm, v(-11649.01, 2124.86) * mm, v(-11651.12, 2143.34) * mm, v(-11654.88, 2166.3) * mm, v(-11661.14, 2193.54) * mm, v(-11669.12, 2220.46) * mm, v(-11682.04, 2255.84) * mm, v(-11702.37, 2298.98) * mm, v(-11728.1, 2340.39) * mm, v(-11751.83, 2372.28) * mm, v(-11771.17, 2395.53) * mm, v(-11792.02, 2418.09) * mm, v(-11810.63, 2436.25) * mm, v(-11826.25, 2450.4) * mm, v(-11838.33, 2460.79) * mm, v(-11848.7, 2469.28) * mm, v(-11857.17, 2475.96) * mm, v(-11863.61, 2480.92) * mm, v(-11870.13, 2485.82) * mm, v(-11878.92, 2492.25) * mm, v(-11890.08, 2500.13) * mm, v(-11903.75, 2509.3) * mm, v(-11922.32, 2521.16) * mm, v(-11946.18, 2535.29) * mm, v(-11975.77, 2551.1) * mm, v(-12006.26, 2565.74) * mm, v(-12048.05, 2583.7) * mm, v(-12102.24, 2603.17) * mm, v(-12158.65, 2618.53) * mm, v(-12204.87, 2628.28) * mm, v(-12240.01, 2634.31) * mm, v(-12275.59, 2639.03) * mm, v(-12305.54, 2641.86) * mm, v(-12329.65, 2643.45) * mm, v(-12347.8, 2644.3) * mm, v(-12362.98, 2644.74) * mm, v(-12375.15, 2644.91) * mm, v(-12384.3, 2644.95) * mm, v(-12393.44, 2644.91) * mm, v(-12405.6, 2644.74) * mm, v(-12420.79, 2644.3) * mm, v(-12438.94, 2643.45) * mm, v(-12463.05, 2641.86) * mm, v(-12493, 2639.03) * mm, v(-12528.58, 2634.31) * mm, v(-12563.72, 2628.28) * mm, v(-12609.94, 2618.53) * mm, v(-12666.35, 2603.17) * mm, v(-12720.54, 2583.7) * mm, v(-12762.33, 2565.74) * mm, v(-12792.82, 2551.1) * mm, v(-12822.41, 2535.29) * mm, v(-12846.27, 2521.16) * mm, v(-12864.84, 2509.3) * mm, v(-12878.5, 2500.13) * mm, v(-12889.67, 2492.25) * mm, v(-12898.45, 2485.82) * mm, v(-12904.98, 2480.92) * mm, v(-12911.42, 2475.96) * mm, v(-12919.9, 2469.28) * mm, v(-12930.26, 2460.79) * mm, v(-12942.34, 2450.4) * mm, v(-12957.96, 2436.25) * mm, v(-12976.57, 2418.09) * mm, v(-12997.42, 2395.53) * mm, v(-13016.76, 2372.28) * mm, v(-13040.48, 2340.39) * mm, v(-13066.22, 2298.98) * mm, v(-13086.55, 2255.84) * mm, v(-13099.47, 2220.46) * mm, v(-13107.45, 2193.54) * mm, v(-13113.71, 2166.3) * mm, v(-13117.46, 2143.34) * mm, v(-13119.58, 2124.86) * mm, v(-13120.71, 2110.94) * mm, v(-13121.28, 2099.3) * mm, v(-13121.5, 2089.98) * mm, v(-13121.57, 2082.97) * mm, v(-13121.5, 2075.96) * mm], "construction": true});
            skFitSpline(sketch, "E42.trimOffspring", {"points": [v(-13121.5, 2089.98) * mm, v(-13121.57, 2082.97) * mm, v(-13121.5, 2075.96) * mm, v(-13121.28, 2066.63) * mm, v(-13120.71, 2055) * mm, v(-13119.58, 2041.08) * mm, v(-13117.46, 2022.6) * mm, v(-13113.71, 1999.65) * mm, v(-13107.45, 1972.4) * mm, v(-13099.47, 1945.48) * mm, v(-13086.55, 1910.1) * mm, v(-13066.22, 1866.96) * mm, v(-13040.48, 1825.56) * mm, v(-13016.76, 1793.67) * mm, v(-12997.42, 1770.4) * mm, v(-12976.57, 1747.86) * mm, v(-12957.96, 1729.69) * mm, v(-12942.34, 1715.55) * mm, v(-12930.26, 1705.16) * mm, v(-12919.9, 1696.67) * mm, v(-12911.42, 1689.98) * mm, v(-12904.98, 1685.02) * mm, v(-12898.45, 1680.13) * mm, v(-12889.67, 1673.69) * mm, v(-12878.5, 1665.81) * mm, v(-12864.84, 1656.64) * mm, v(-12846.27, 1644.78) * mm, v(-12822.41, 1630.66) * mm, v(-12792.82, 1614.85) * mm, v(-12762.33, 1600.2) * mm, v(-12720.54, 1582.24) * mm, v(-12666.35, 1562.77) * mm, v(-12609.94, 1547.4) * mm, v(-12563.72, 1537.66) * mm, v(-12528.58, 1531.63) * mm, v(-12493, 1526.91) * mm, v(-12463.05, 1524.08) * mm, v(-12438.94, 1522.49) * mm, v(-12420.79, 1521.63) * mm, v(-12405.6, 1521.2) * mm, v(-12393.44, 1521.03) * mm, v(-12384.3, 1520.99) * mm, v(-12375.15, 1521.03) * mm, v(-12362.98, 1521.2) * mm, v(-12347.8, 1521.63) * mm, v(-12329.65, 1522.49) * mm, v(-12305.54, 1524.08) * mm, v(-12275.59, 1526.91) * mm, v(-12240.01, 1531.63) * mm, v(-12204.87, 1537.66) * mm, v(-12158.65, 1547.4) * mm, v(-12102.24, 1562.77) * mm, v(-12048.05, 1582.24) * mm, v(-12006.26, 1600.2) * mm, v(-11975.77, 1614.85) * mm, v(-11946.18, 1630.66) * mm, v(-11922.32, 1644.78) * mm, v(-11903.75, 1656.64) * mm, v(-11890.08, 1665.81) * mm, v(-11878.92, 1673.69) * mm, v(-11870.13, 1680.13) * mm, v(-11863.61, 1685.02) * mm, v(-11857.17, 1689.98) * mm, v(-11848.7, 1696.67) * mm, v(-11838.33, 1705.16) * mm, v(-11826.25, 1715.55) * mm, v(-11810.63, 1729.69) * mm, v(-11792.02, 1747.86) * mm, v(-11771.17, 1770.4) * mm, v(-11751.83, 1793.67) * mm, v(-11728.1, 1825.56) * mm, v(-11702.37, 1866.96) * mm, v(-11682.04, 1910.1) * mm, v(-11669.12, 1945.48) * mm, v(-11661.14, 1972.4) * mm, v(-11654.88, 1999.65) * mm, v(-11651.12, 2022.6) * mm, v(-11649.01, 2041.08) * mm, v(-11647.88, 2055) * mm, v(-11647.3, 2066.63) * mm, v(-11647.08, 2075.96) * mm, v(-11647.02, 2082.97) * mm, v(-11647.08, 2089.98) * mm, v(-11647.3, 2099.3) * mm, v(-11647.88, 2110.94) * mm, v(-11649.01, 2124.86) * mm, v(-11651.12, 2143.34) * mm, v(-11654.88, 2166.3) * mm, v(-11661.14, 2193.54) * mm, v(-11669.12, 2220.46) * mm, v(-11682.04, 2255.84) * mm, v(-11702.37, 2298.98) * mm, v(-11728.1, 2340.39) * mm, v(-11751.83, 2372.28) * mm, v(-11771.17, 2395.53) * mm, v(-11792.02, 2418.09) * mm, v(-11810.63, 2436.25) * mm, v(-11826.25, 2450.4) * mm, v(-11838.33, 2460.79) * mm, v(-11848.7, 2469.28) * mm, v(-11857.17, 2475.96) * mm, v(-11863.61, 2480.92) * mm, v(-11870.13, 2485.82) * mm, v(-11878.92, 2492.25) * mm, v(-11890.08, 2500.13) * mm, v(-11903.75, 2509.3) * mm, v(-11922.32, 2521.16) * mm, v(-11946.18, 2535.29) * mm, v(-11975.77, 2551.1) * mm, v(-12006.26, 2565.74) * mm, v(-12048.05, 2583.7) * mm, v(-12102.24, 2603.17) * mm, v(-12158.65, 2618.53) * mm, v(-12204.87, 2628.28) * mm, v(-12240.01, 2634.31) * mm, v(-12275.59, 2639.03) * mm, v(-12305.54, 2641.86) * mm, v(-12329.65, 2643.45) * mm, v(-12347.8, 2644.3) * mm, v(-12362.98, 2644.74) * mm, v(-12375.15, 2644.91) * mm, v(-12384.3, 2644.95) * mm, v(-12393.44, 2644.91) * mm, v(-12405.6, 2644.74) * mm, v(-12420.79, 2644.3) * mm, v(-12438.94, 2643.45) * mm, v(-12463.05, 2641.86) * mm, v(-12493, 2639.03) * mm, v(-12528.58, 2634.31) * mm, v(-12563.72, 2628.28) * mm, v(-12609.94, 2618.53) * mm, v(-12666.35, 2603.17) * mm, v(-12720.54, 2583.7) * mm, v(-12762.33, 2565.74) * mm, v(-12792.82, 2551.1) * mm, v(-12822.41, 2535.29) * mm, v(-12846.27, 2521.16) * mm, v(-12864.84, 2509.3) * mm, v(-12878.5, 2500.13) * mm, v(-12889.67, 2492.25) * mm, v(-12898.45, 2485.82) * mm, v(-12904.98, 2480.92) * mm, v(-12911.42, 2475.96) * mm, v(-12919.9, 2469.28) * mm, v(-12930.26, 2460.79) * mm, v(-12942.34, 2450.4) * mm, v(-12957.96, 2436.25) * mm, v(-12976.57, 2418.09) * mm, v(-12997.42, 2395.53) * mm, v(-13016.76, 2372.28) * mm, v(-13040.48, 2340.39) * mm, v(-13066.22, 2298.98) * mm, v(-13086.55, 2255.84) * mm, v(-13099.47, 2220.46) * mm, v(-13107.45, 2193.54) * mm, v(-13113.71, 2166.3) * mm, v(-13117.46, 2143.34) * mm, v(-13119.58, 2124.86) * mm, v(-13120.71, 2110.94) * mm, v(-13121.28, 2099.3) * mm, v(-13121.5, 2089.98) * mm, v(-13121.57, 2082.97) * mm, v(-13121.5, 2075.96) * mm], "construction": true});
            skArc(sketch, "E43", {"start": v(-11898.95, 2490.78) * mm, "mid": v(-11897.47, 2490) * mm, "end": v(-11896, 2489.21) * mm, "construction": true});
            skArc(sketch, "E44", {"start": v(-11898.95, 1675.16) * mm, "mid": v(-11897.47, 1675.94) * mm, "end": v(-11896, 1676.74) * mm, "construction": true});
            skArc(sketch, "E45", {"start": v(-11896, 2489.21) * mm, "mid": v(-12115.88, 2082.97) * mm, "end": v(-11896, 1676.74) * mm, "construction": true});
            skLineSegment(sketch, "E46", {"start": v(-11896, 2489.21) * mm, "end": v(-11896, 1676.74) * mm, "construction": true});
            skArc(sketch, "E47", {"start": v(-12810.9, 2011.02) * mm, "mid": v(-12498.5, 1670.75) * mm, "end": v(-12042.79, 1746.23) * mm, "construction": true});
            skLineSegment(sketch, "E48", {"start": v(-12810.9, 2011.02) * mm, "end": v(-12042.79, 1746.23) * mm, "construction": true});
            skArc(sketch, "E49", {"start": v(-8122.77, 418.94) * mm, "mid": v(-8342.65, 12.7) * mm, "end": v(-8122.77, -393.54) * mm});
            skPoint(sketch, "E50", {"position": v(-8122.77, 12.7) * mm});
            skSolve(sketch);
        }
        {
            var Q0;
            Q0=qCreatedBy(id+"F5.planeOp",FACE);
            var sketch = newSketch(context, id + "F7", { "sketchPlane" : qUnion([Q0])});
            skLineSegment(sketch, "E51.0.0", {"start": v(-10752.89, -2367.65) * mm, "end": v(-9533.69, -2367.65) * mm, "construction": true});
            skLineSegment(sketch, "E52.2", {"start": v(-9533.69, -2367.65) * mm, "end": v(-9533.69, -1148.45) * mm, "construction": true});
            skLineSegment(sketch, "E52.1", {"start": v(-9533.69, -1148.45) * mm, "end": v(-10752.89, -1148.45) * mm, "construction": true});
            skLineSegment(sketch, "E52.0", {"start": v(-10752.89, -2367.65) * mm, "end": v(-10752.89, -1148.45) * mm, "construction": true});
            skFitSpline(sketch, "E53.0", {"points": [v(-10759.2, -1697.06) * mm, v(-10759.26, -1704.07) * mm, v(-10759.2, -1711.08) * mm, v(-10758.97, -1720.4) * mm, v(-10758.4, -1732.04) * mm, v(-10757.27, -1745.96) * mm, v(-10755.15, -1764.44) * mm, v(-10751.4, -1787.4) * mm, v(-10745.14, -1814.64) * mm, v(-10737.16, -1841.56) * mm, v(-10724.24, -1876.94) * mm, v(-10703.9, -1920.08) * mm, v(-10678.17, -1961.49) * mm, v(-10654.45, -1993.38) * mm, v(-10635.11, -2016.64) * mm, v(-10614.26, -2039.19) * mm, v(-10595.65, -2057.35) * mm, v(-10580.03, -2071.5) * mm, v(-10567.95, -2081.89) * mm, v(-10557.58, -2090.38) * mm, v(-10549.11, -2097.06) * mm, v(-10542.67, -2102.02) * mm, v(-10536.14, -2106.92) * mm, v(-10527.36, -2113.35) * mm, v(-10516.2, -2121.23) * mm, v(-10502.53, -2130.4) * mm, v(-10483.96, -2142.26) * mm, v(-10460.1, -2156.39) * mm, v(-10430.51, -2172.2) * mm, v(-10400.02, -2186.85) * mm, v(-10358.23, -2204.8) * mm, v(-10304.04, -2224.27) * mm, v(-10247.63, -2239.63) * mm, v(-10201.41, -2249.38) * mm, v(-10166.27, -2255.41) * mm, v(-10130.7, -2260.13) * mm, v(-10100.74, -2262.96) * mm, v(-10076.63, -2264.55) * mm, v(-10058.48, -2265.41) * mm, v(-10043.3, -2265.84) * mm, v(-10031.13, -2266.01) * mm, v(-10021.98, -2266.06) * mm, v(-10012.84, -2266.01) * mm, v(-10000.67, -2265.84) * mm, v(-9985.5, -2265.41) * mm, v(-9967.34, -2264.55) * mm, v(-9943.23, -2262.96) * mm, v(-9913.28, -2260.13) * mm, v(-9877.7, -2255.41) * mm, v(-9842.56, -2249.38) * mm, v(-9796.34, -2239.63) * mm, v(-9739.93, -2224.27) * mm, v(-9685.74, -2204.8) * mm, v(-9643.95, -2186.85) * mm, v(-9613.46, -2172.2) * mm, v(-9583.87, -2156.39) * mm, v(-9560.01, -2142.26) * mm, v(-9541.44, -2130.4) * mm, v(-9527.77, -2121.23) * mm, v(-9516.61, -2113.35) * mm, v(-9507.82, -2106.92) * mm, v(-9501.3, -2102.02) * mm, v(-9494.86, -2097.06) * mm, v(-9486.39, -2090.38) * mm, v(-9476.02, -2081.89) * mm, v(-9463.94, -2071.5) * mm, v(-9448.32, -2057.35) * mm, v(-9429.7, -2039.19) * mm, v(-9408.86, -2016.64) * mm, v(-9389.52, -1993.38) * mm, v(-9365.8, -1961.49) * mm, v(-9340.06, -1920.08) * mm, v(-9319.73, -1876.94) * mm, v(-9306.81, -1841.56) * mm, v(-9298.83, -1814.64) * mm, v(-9292.57, -1787.4) * mm, v(-9288.82, -1764.44) * mm, v(-9286.7, -1745.96) * mm, v(-9285.57, -1732.04) * mm, v(-9285, -1720.4) * mm, v(-9284.77, -1711.08) * mm, v(-9284.71, -1704.07) * mm, v(-9284.77, -1697.06) * mm, v(-9285, -1687.74) * mm, v(-9285.57, -1676.1) * mm, v(-9286.7, -1662.19) * mm, v(-9288.82, -1643.7) * mm, v(-9292.57, -1620.75) * mm, v(-9298.83, -1593.5) * mm, v(-9306.81, -1566.58) * mm, v(-9319.73, -1531.2) * mm, v(-9340.06, -1488.06) * mm, v(-9365.8, -1446.66) * mm, v(-9389.52, -1414.77) * mm, v(-9408.86, -1391.5) * mm, v(-9429.7, -1368.96) * mm, v(-9448.32, -1350.79) * mm, v(-9463.94, -1336.65) * mm, v(-9476.02, -1326.26) * mm, v(-9486.39, -1317.77) * mm, v(-9494.86, -1311.08) * mm, v(-9501.3, -1306.12) * mm, v(-9507.82, -1301.23) * mm, v(-9516.61, -1294.8) * mm, v(-9527.77, -1286.91) * mm, v(-9541.44, -1277.74) * mm, v(-9560.01, -1265.88) * mm, v(-9583.87, -1251.76) * mm, v(-9613.46, -1235.95) * mm, v(-9643.95, -1221.3) * mm, v(-9685.74, -1203.34) * mm, v(-9739.93, -1183.87) * mm, v(-9796.34, -1168.51) * mm, v(-9842.56, -1158.76) * mm, v(-9877.7, -1152.73) * mm, v(-9913.28, -1148.01) * mm, v(-9943.23, -1145.18) * mm, v(-9967.34, -1143.59) * mm, v(-9985.5, -1142.73) * mm, v(-10000.67, -1142.3) * mm, v(-10012.84, -1142.13) * mm, v(-10021.98, -1142.09) * mm, v(-10031.13, -1142.13) * mm, v(-10043.3, -1142.3) * mm, v(-10058.48, -1142.73) * mm, v(-10076.63, -1143.59) * mm, v(-10100.74, -1145.18) * mm, v(-10130.7, -1148.01) * mm, v(-10166.27, -1152.73) * mm, v(-10201.41, -1158.76) * mm, v(-10247.63, -1168.51) * mm, v(-10304.04, -1183.87) * mm, v(-10358.23, -1203.34) * mm, v(-10400.02, -1221.3) * mm, v(-10430.51, -1235.95) * mm, v(-10460.1, -1251.76) * mm, v(-10483.96, -1265.88) * mm, v(-10502.53, -1277.74) * mm, v(-10516.2, -1286.91) * mm, v(-10527.36, -1294.8) * mm, v(-10536.14, -1301.23) * mm, v(-10542.67, -1306.12) * mm, v(-10549.11, -1311.08) * mm, v(-10557.58, -1317.77) * mm, v(-10567.95, -1326.26) * mm, v(-10580.03, -1336.65) * mm, v(-10595.65, -1350.79) * mm, v(-10614.26, -1368.96) * mm, v(-10635.11, -1391.5) * mm, v(-10654.45, -1414.77) * mm, v(-10678.17, -1446.66) * mm, v(-10703.9, -1488.06) * mm, v(-10724.24, -1531.2) * mm, v(-10737.16, -1566.58) * mm, v(-10745.14, -1593.5) * mm, v(-10751.4, -1620.75) * mm, v(-10755.15, -1643.7) * mm, v(-10757.27, -1662.19) * mm, v(-10758.4, -1676.1) * mm, v(-10758.97, -1687.74) * mm, v(-10759.2, -1697.06) * mm, v(-10759.26, -1704.07) * mm, v(-10759.2, -1711.08) * mm], "construction": true});
            skFitSpline(sketch, "E54.0", {"points": [v(-9263.64, -1710.08) * mm, v(-9263.6, -1704.07) * mm, v(-9263.64, -1698.06) * mm, v(-9263.83, -1690.06) * mm, v(-9264.28, -1680.08) * mm, v(-9265.19, -1668.14) * mm, v(-9266.88, -1652.28) * mm, v(-9269.88, -1632.59) * mm, v(-9274.88, -1609.2) * mm, v(-9281.27, -1586.07) * mm, v(-9291.6, -1555.67) * mm, v(-9307.9, -1518.55) * mm, v(-9328.54, -1482.87) * mm, v(-9347.6, -1455.36) * mm, v(-9363.14, -1435.27) * mm, v(-9379.92, -1415.78) * mm, v(-9394.91, -1400.07) * mm, v(-9407.5, -1387.84) * mm, v(-9417.24, -1378.84) * mm, v(-9425.6, -1371.49) * mm, v(-9432.43, -1365.7) * mm, v(-9437.63, -1361.4) * mm, v(-9442.9, -1357.15) * mm, v(-9449.99, -1351.58) * mm, v(-9459, -1344.75) * mm, v(-9470.03, -1336.8) * mm, v(-9485.04, -1326.5) * mm, v(-9504.32, -1314.24) * mm, v(-9528.25, -1300.51) * mm, v(-9552.92, -1287.79) * mm, v(-9586.74, -1272.17) * mm, v(-9630.64, -1255.24) * mm, v(-9676.36, -1241.87) * mm, v(-9713.84, -1233.37) * mm, v(-9742.35, -1228.13) * mm, v(-9771.2, -1224.01) * mm, v(-9795.5, -1221.55) * mm, v(-9815.06, -1220.16) * mm, v(-9829.8, -1219.41) * mm, v(-9842.1, -1219.04) * mm, v(-9851.98, -1218.9) * mm, v(-9859.4, -1218.85) * mm, v(-9866.82, -1218.9) * mm, v(-9876.7, -1219.04) * mm, v(-9889, -1219.41) * mm, v(-9903.74, -1220.16) * mm, v(-9923.3, -1221.55) * mm, v(-9947.6, -1224.01) * mm, v(-9976.45, -1228.13) * mm, v(-10004.96, -1233.37) * mm, v(-10042.44, -1241.87) * mm, v(-10088.16, -1255.24) * mm, v(-10132.06, -1272.17) * mm, v(-10165.88, -1287.79) * mm, v(-10190.55, -1300.51) * mm, v(-10214.48, -1314.24) * mm, v(-10233.76, -1326.5) * mm, v(-10248.77, -1336.8) * mm, v(-10259.8, -1344.75) * mm, v(-10268.81, -1351.58) * mm, v(-10275.9, -1357.15) * mm, v(-10281.17, -1361.4) * mm, v(-10286.37, -1365.7) * mm, v(-10293.2, -1371.49) * mm, v(-10301.56, -1378.84) * mm, v(-10311.3, -1387.84) * mm, v(-10323.89, -1400.07) * mm, v(-10338.88, -1415.78) * mm, v(-10355.66, -1435.27) * mm, v(-10371.2, -1455.36) * mm, v(-10390.26, -1482.87) * mm, v(-10410.9, -1518.55) * mm, v(-10427.2, -1555.67) * mm, v(-10437.53, -1586.07) * mm, v(-10443.92, -1609.2) * mm, v(-10448.93, -1632.59) * mm, v(-10451.92, -1652.28) * mm, v(-10453.61, -1668.14) * mm, v(-10454.52, -1680.08) * mm, v(-10454.97, -1690.06) * mm, v(-10455.16, -1698.06) * mm, v(-10455.2, -1704.07) * mm, v(-10455.16, -1710.08) * mm, v(-10454.97, -1718.09) * mm, v(-10454.52, -1728.07) * mm, v(-10453.61, -1740) * mm, v(-10451.92, -1755.86) * mm, v(-10448.93, -1775.56) * mm, v(-10443.92, -1798.95) * mm, v(-10437.53, -1822.07) * mm, v(-10427.2, -1852.48) * mm, v(-10410.9, -1889.6) * mm, v(-10390.26, -1925.27) * mm, v(-10371.2, -1952.79) * mm, v(-10355.66, -1972.87) * mm, v(-10338.88, -1992.36) * mm, v(-10323.89, -2008.07) * mm, v(-10311.3, -2020.3) * mm, v(-10301.56, -2029.3) * mm, v(-10293.2, -2036.66) * mm, v(-10286.37, -2042.45) * mm, v(-10281.17, -2046.74) * mm, v(-10275.9, -2050.99) * mm, v(-10268.81, -2056.57) * mm, v(-10259.8, -2063.4) * mm, v(-10248.77, -2071.35) * mm, v(-10233.76, -2081.64) * mm, v(-10214.48, -2093.9) * mm, v(-10190.55, -2107.63) * mm, v(-10165.88, -2120.36) * mm, v(-10132.06, -2135.97) * mm, v(-10088.16, -2152.9) * mm, v(-10042.44, -2166.28) * mm, v(-10004.96, -2174.77) * mm, v(-9976.45, -2180.02) * mm, v(-9947.6, -2184.13) * mm, v(-9923.3, -2186.6) * mm, v(-9903.74, -2187.98) * mm, v(-9889, -2188.73) * mm, v(-9876.7, -2189.1) * mm, v(-9866.82, -2189.25) * mm, v(-9859.4, -2189.3) * mm, v(-9851.98, -2189.25) * mm, v(-9842.1, -2189.1) * mm, v(-9829.8, -2188.73) * mm, v(-9815.06, -2187.98) * mm, v(-9795.5, -2186.6) * mm, v(-9771.2, -2184.13) * mm, v(-9742.35, -2180.02) * mm, v(-9713.84, -2174.77) * mm, v(-9676.36, -2166.28) * mm, v(-9630.64, -2152.9) * mm, v(-9586.74, -2135.97) * mm, v(-9552.92, -2120.36) * mm, v(-9528.25, -2107.63) * mm, v(-9504.32, -2093.9) * mm, v(-9485.04, -2081.64) * mm, v(-9470.03, -2071.35) * mm, v(-9459, -2063.4) * mm, v(-9449.99, -2056.57) * mm, v(-9442.9, -2050.99) * mm, v(-9437.63, -2046.74) * mm, v(-9432.43, -2042.45) * mm, v(-9425.6, -2036.66) * mm, v(-9417.24, -2029.3) * mm, v(-9407.5, -2020.3) * mm, v(-9394.91, -2008.07) * mm, v(-9379.92, -1992.36) * mm, v(-9363.14, -1972.87) * mm, v(-9347.6, -1952.79) * mm, v(-9328.54, -1925.27) * mm, v(-9307.9, -1889.6) * mm, v(-9291.6, -1852.48) * mm, v(-9281.27, -1822.07) * mm, v(-9274.88, -1798.95) * mm, v(-9269.88, -1775.56) * mm, v(-9266.88, -1755.86) * mm, v(-9265.19, -1740) * mm, v(-9264.28, -1728.07) * mm, v(-9263.83, -1718.09) * mm, v(-9263.64, -1710.08) * mm, v(-9263.6, -1704.07) * mm, v(-9263.64, -1698.06) * mm], "construction": true});
            skFitSpline(sketch, "E55.0", {"points": [v(-10759.2, -1697.06) * mm, v(-10759.26, -1704.07) * mm, v(-10759.2, -1711.08) * mm, v(-10758.97, -1720.4) * mm, v(-10758.4, -1732.04) * mm, v(-10757.27, -1745.96) * mm, v(-10755.15, -1764.44) * mm, v(-10751.4, -1787.4) * mm, v(-10745.14, -1814.64) * mm, v(-10737.16, -1841.56) * mm, v(-10724.24, -1876.94) * mm, v(-10703.9, -1920.08) * mm, v(-10678.17, -1961.49) * mm, v(-10654.45, -1993.38) * mm, v(-10635.11, -2016.64) * mm, v(-10614.26, -2039.19) * mm, v(-10595.65, -2057.35) * mm, v(-10580.03, -2071.5) * mm, v(-10567.95, -2081.89) * mm, v(-10557.58, -2090.38) * mm, v(-10549.11, -2097.06) * mm, v(-10542.67, -2102.02) * mm, v(-10536.14, -2106.92) * mm, v(-10527.36, -2113.35) * mm, v(-10516.2, -2121.23) * mm, v(-10502.53, -2130.4) * mm, v(-10483.96, -2142.26) * mm, v(-10460.1, -2156.39) * mm, v(-10430.51, -2172.2) * mm, v(-10400.02, -2186.85) * mm, v(-10358.23, -2204.8) * mm, v(-10304.04, -2224.27) * mm, v(-10247.63, -2239.63) * mm, v(-10201.41, -2249.38) * mm, v(-10166.27, -2255.41) * mm, v(-10130.7, -2260.13) * mm, v(-10100.74, -2262.96) * mm, v(-10076.63, -2264.55) * mm, v(-10058.48, -2265.41) * mm, v(-10043.3, -2265.84) * mm, v(-10031.13, -2266.01) * mm, v(-10021.98, -2266.06) * mm, v(-10012.84, -2266.01) * mm, v(-10000.67, -2265.84) * mm, v(-9985.5, -2265.41) * mm, v(-9967.34, -2264.55) * mm, v(-9943.23, -2262.96) * mm, v(-9913.28, -2260.13) * mm, v(-9877.7, -2255.41) * mm, v(-9842.56, -2249.38) * mm, v(-9796.34, -2239.63) * mm, v(-9739.93, -2224.27) * mm, v(-9685.74, -2204.8) * mm, v(-9643.95, -2186.85) * mm, v(-9613.46, -2172.2) * mm, v(-9583.87, -2156.39) * mm, v(-9560.01, -2142.26) * mm, v(-9541.44, -2130.4) * mm, v(-9527.77, -2121.23) * mm, v(-9516.61, -2113.35) * mm, v(-9507.82, -2106.92) * mm, v(-9501.3, -2102.02) * mm, v(-9494.86, -2097.06) * mm, v(-9486.39, -2090.38) * mm, v(-9476.02, -2081.89) * mm, v(-9463.94, -2071.5) * mm, v(-9448.32, -2057.35) * mm, v(-9429.7, -2039.19) * mm, v(-9408.86, -2016.64) * mm, v(-9389.52, -1993.38) * mm, v(-9365.8, -1961.49) * mm, v(-9340.06, -1920.08) * mm, v(-9319.73, -1876.94) * mm, v(-9306.81, -1841.56) * mm, v(-9298.83, -1814.64) * mm, v(-9292.57, -1787.4) * mm, v(-9288.82, -1764.44) * mm, v(-9286.7, -1745.96) * mm, v(-9285.57, -1732.04) * mm, v(-9285, -1720.4) * mm, v(-9284.77, -1711.08) * mm, v(-9284.71, -1704.07) * mm, v(-9284.77, -1697.06) * mm, v(-9285, -1687.74) * mm, v(-9285.57, -1676.1) * mm, v(-9286.7, -1662.19) * mm, v(-9288.82, -1643.7) * mm, v(-9292.57, -1620.75) * mm, v(-9298.83, -1593.5) * mm, v(-9306.81, -1566.58) * mm, v(-9319.73, -1531.2) * mm, v(-9340.06, -1488.06) * mm, v(-9365.8, -1446.66) * mm, v(-9389.52, -1414.77) * mm, v(-9408.86, -1391.5) * mm, v(-9429.7, -1368.96) * mm, v(-9448.32, -1350.79) * mm, v(-9463.94, -1336.65) * mm, v(-9476.02, -1326.26) * mm, v(-9486.39, -1317.77) * mm, v(-9494.86, -1311.08) * mm, v(-9501.3, -1306.12) * mm, v(-9507.82, -1301.23) * mm, v(-9516.61, -1294.8) * mm, v(-9527.77, -1286.91) * mm, v(-9541.44, -1277.74) * mm, v(-9560.01, -1265.88) * mm, v(-9583.87, -1251.76) * mm, v(-9613.46, -1235.95) * mm, v(-9643.95, -1221.3) * mm, v(-9685.74, -1203.34) * mm, v(-9739.93, -1183.87) * mm, v(-9796.34, -1168.51) * mm, v(-9842.56, -1158.76) * mm, v(-9877.7, -1152.73) * mm, v(-9913.28, -1148.01) * mm, v(-9943.23, -1145.18) * mm, v(-9967.34, -1143.59) * mm, v(-9985.5, -1142.73) * mm, v(-10000.67, -1142.3) * mm, v(-10012.84, -1142.13) * mm, v(-10021.98, -1142.09) * mm, v(-10031.13, -1142.13) * mm, v(-10043.3, -1142.3) * mm, v(-10058.48, -1142.73) * mm, v(-10076.63, -1143.59) * mm, v(-10100.74, -1145.18) * mm, v(-10130.7, -1148.01) * mm, v(-10166.27, -1152.73) * mm, v(-10201.41, -1158.76) * mm, v(-10247.63, -1168.51) * mm, v(-10304.04, -1183.87) * mm, v(-10358.23, -1203.34) * mm, v(-10400.02, -1221.3) * mm, v(-10430.51, -1235.95) * mm, v(-10460.1, -1251.76) * mm, v(-10483.96, -1265.88) * mm, v(-10502.53, -1277.74) * mm, v(-10516.2, -1286.91) * mm, v(-10527.36, -1294.8) * mm, v(-10536.14, -1301.23) * mm, v(-10542.67, -1306.12) * mm, v(-10549.11, -1311.08) * mm, v(-10557.58, -1317.77) * mm, v(-10567.95, -1326.26) * mm, v(-10580.03, -1336.65) * mm, v(-10595.65, -1350.79) * mm, v(-10614.26, -1368.96) * mm, v(-10635.11, -1391.5) * mm, v(-10654.45, -1414.77) * mm, v(-10678.17, -1446.66) * mm, v(-10703.9, -1488.06) * mm, v(-10724.24, -1531.2) * mm, v(-10737.16, -1566.58) * mm, v(-10745.14, -1593.5) * mm, v(-10751.4, -1620.75) * mm, v(-10755.15, -1643.7) * mm, v(-10757.27, -1662.19) * mm, v(-10758.4, -1676.1) * mm, v(-10758.97, -1687.74) * mm, v(-10759.2, -1697.06) * mm, v(-10759.26, -1704.07) * mm, v(-10759.2, -1711.08) * mm], "construction": true});
            skArc(sketch, "E56.0", {"start": v(-9533.69, -2359.86) * mm, "mid": v(-9649.36, -2288.77) * mm, "end": v(-9773.2, -2233.1) * mm, "construction": true});
            skArc(sketch, "E57.0", {"start": v(-10383.61, -2193.83) * mm, "mid": v(-10576.28, -2258.98) * mm, "end": v(-10752.89, -2359.86) * mm, "construction": true});
            skFitSpline(sketch, "E58.trimOffspring", {"points": [v(-10759.2, -1697.06) * mm, v(-10759.26, -1704.07) * mm, v(-10759.2, -1711.08) * mm, v(-10758.97, -1720.4) * mm, v(-10758.4, -1732.04) * mm, v(-10757.27, -1745.96) * mm, v(-10755.15, -1764.44) * mm, v(-10751.4, -1787.4) * mm, v(-10745.14, -1814.64) * mm, v(-10737.16, -1841.56) * mm, v(-10724.24, -1876.94) * mm, v(-10703.9, -1920.08) * mm, v(-10678.17, -1961.49) * mm, v(-10654.45, -1993.38) * mm, v(-10635.11, -2016.64) * mm, v(-10614.26, -2039.19) * mm, v(-10595.65, -2057.35) * mm, v(-10580.03, -2071.5) * mm, v(-10567.95, -2081.89) * mm, v(-10557.58, -2090.38) * mm, v(-10549.11, -2097.06) * mm, v(-10542.67, -2102.02) * mm, v(-10536.14, -2106.92) * mm, v(-10527.36, -2113.35) * mm, v(-10516.2, -2121.23) * mm, v(-10502.53, -2130.4) * mm, v(-10483.96, -2142.26) * mm, v(-10460.1, -2156.39) * mm, v(-10430.51, -2172.2) * mm, v(-10400.02, -2186.85) * mm, v(-10358.23, -2204.8) * mm, v(-10304.04, -2224.27) * mm, v(-10247.63, -2239.63) * mm, v(-10201.41, -2249.38) * mm, v(-10166.27, -2255.41) * mm, v(-10130.7, -2260.13) * mm, v(-10100.74, -2262.96) * mm, v(-10076.63, -2264.55) * mm, v(-10058.48, -2265.41) * mm, v(-10043.3, -2265.84) * mm, v(-10031.13, -2266.01) * mm, v(-10021.98, -2266.06) * mm, v(-10012.84, -2266.01) * mm, v(-10000.67, -2265.84) * mm, v(-9985.5, -2265.41) * mm, v(-9967.34, -2264.55) * mm, v(-9943.23, -2262.96) * mm, v(-9913.28, -2260.13) * mm, v(-9877.7, -2255.41) * mm, v(-9842.56, -2249.38) * mm, v(-9796.34, -2239.63) * mm, v(-9739.93, -2224.27) * mm, v(-9685.74, -2204.8) * mm, v(-9643.95, -2186.85) * mm, v(-9613.46, -2172.2) * mm, v(-9583.87, -2156.39) * mm, v(-9560.01, -2142.26) * mm, v(-9541.44, -2130.4) * mm, v(-9527.77, -2121.23) * mm, v(-9516.61, -2113.35) * mm, v(-9507.82, -2106.92) * mm, v(-9501.3, -2102.02) * mm, v(-9494.86, -2097.06) * mm, v(-9486.39, -2090.38) * mm, v(-9476.02, -2081.89) * mm, v(-9463.94, -2071.5) * mm, v(-9448.32, -2057.35) * mm, v(-9429.7, -2039.19) * mm, v(-9408.86, -2016.64) * mm, v(-9389.52, -1993.38) * mm, v(-9365.8, -1961.49) * mm, v(-9340.06, -1920.08) * mm, v(-9319.73, -1876.94) * mm, v(-9306.81, -1841.56) * mm, v(-9298.83, -1814.64) * mm, v(-9292.57, -1787.4) * mm, v(-9288.82, -1764.44) * mm, v(-9286.7, -1745.96) * mm, v(-9285.57, -1732.04) * mm, v(-9285, -1720.4) * mm, v(-9284.77, -1711.08) * mm, v(-9284.71, -1704.07) * mm, v(-9284.77, -1697.06) * mm, v(-9285, -1687.74) * mm, v(-9285.57, -1676.1) * mm, v(-9286.7, -1662.19) * mm, v(-9288.82, -1643.7) * mm, v(-9292.57, -1620.75) * mm, v(-9298.83, -1593.5) * mm, v(-9306.81, -1566.58) * mm, v(-9319.73, -1531.2) * mm, v(-9340.06, -1488.06) * mm, v(-9365.8, -1446.66) * mm, v(-9389.52, -1414.77) * mm, v(-9408.86, -1391.5) * mm, v(-9429.7, -1368.96) * mm, v(-9448.32, -1350.79) * mm, v(-9463.94, -1336.65) * mm, v(-9476.02, -1326.26) * mm, v(-9486.39, -1317.77) * mm, v(-9494.86, -1311.08) * mm, v(-9501.3, -1306.12) * mm, v(-9507.82, -1301.23) * mm, v(-9516.61, -1294.8) * mm, v(-9527.77, -1286.91) * mm, v(-9541.44, -1277.74) * mm, v(-9560.01, -1265.88) * mm, v(-9583.87, -1251.76) * mm, v(-9613.46, -1235.95) * mm, v(-9643.95, -1221.3) * mm, v(-9685.74, -1203.34) * mm, v(-9739.93, -1183.87) * mm, v(-9796.34, -1168.51) * mm, v(-9842.56, -1158.76) * mm, v(-9877.7, -1152.73) * mm, v(-9913.28, -1148.01) * mm, v(-9943.23, -1145.18) * mm, v(-9967.34, -1143.59) * mm, v(-9985.5, -1142.73) * mm, v(-10000.67, -1142.3) * mm, v(-10012.84, -1142.13) * mm, v(-10021.98, -1142.09) * mm, v(-10031.13, -1142.13) * mm, v(-10043.3, -1142.3) * mm, v(-10058.48, -1142.73) * mm, v(-10076.63, -1143.59) * mm, v(-10100.74, -1145.18) * mm, v(-10130.7, -1148.01) * mm, v(-10166.27, -1152.73) * mm, v(-10201.41, -1158.76) * mm, v(-10247.63, -1168.51) * mm, v(-10304.04, -1183.87) * mm, v(-10358.23, -1203.34) * mm, v(-10400.02, -1221.3) * mm, v(-10430.51, -1235.95) * mm, v(-10460.1, -1251.76) * mm, v(-10483.96, -1265.88) * mm, v(-10502.53, -1277.74) * mm, v(-10516.2, -1286.91) * mm, v(-10527.36, -1294.8) * mm, v(-10536.14, -1301.23) * mm, v(-10542.67, -1306.12) * mm, v(-10549.11, -1311.08) * mm, v(-10557.58, -1317.77) * mm, v(-10567.95, -1326.26) * mm, v(-10580.03, -1336.65) * mm, v(-10595.65, -1350.79) * mm, v(-10614.26, -1368.96) * mm, v(-10635.11, -1391.5) * mm, v(-10654.45, -1414.77) * mm, v(-10678.17, -1446.66) * mm, v(-10703.9, -1488.06) * mm, v(-10724.24, -1531.2) * mm, v(-10737.16, -1566.58) * mm, v(-10745.14, -1593.5) * mm, v(-10751.4, -1620.75) * mm, v(-10755.15, -1643.7) * mm, v(-10757.27, -1662.19) * mm, v(-10758.4, -1676.1) * mm, v(-10758.97, -1687.74) * mm, v(-10759.2, -1697.06) * mm, v(-10759.26, -1704.07) * mm, v(-10759.2, -1711.08) * mm], "construction": true});
            skFitSpline(sketch, "E59.trimOffspring", {"points": [v(-10759.2, -1697.06) * mm, v(-10759.26, -1704.07) * mm, v(-10759.2, -1711.08) * mm, v(-10758.97, -1720.4) * mm, v(-10758.4, -1732.04) * mm, v(-10757.27, -1745.96) * mm, v(-10755.15, -1764.44) * mm, v(-10751.4, -1787.4) * mm, v(-10745.14, -1814.64) * mm, v(-10737.16, -1841.56) * mm, v(-10724.24, -1876.94) * mm, v(-10703.9, -1920.08) * mm, v(-10678.17, -1961.49) * mm, v(-10654.45, -1993.38) * mm, v(-10635.11, -2016.64) * mm, v(-10614.26, -2039.19) * mm, v(-10595.65, -2057.35) * mm, v(-10580.03, -2071.5) * mm, v(-10567.95, -2081.89) * mm, v(-10557.58, -2090.38) * mm, v(-10549.11, -2097.06) * mm, v(-10542.67, -2102.02) * mm, v(-10536.14, -2106.92) * mm, v(-10527.36, -2113.35) * mm, v(-10516.2, -2121.23) * mm, v(-10502.53, -2130.4) * mm, v(-10483.96, -2142.26) * mm, v(-10460.1, -2156.39) * mm, v(-10430.51, -2172.2) * mm, v(-10400.02, -2186.85) * mm, v(-10358.23, -2204.8) * mm, v(-10304.04, -2224.27) * mm, v(-10247.63, -2239.63) * mm, v(-10201.41, -2249.38) * mm, v(-10166.27, -2255.41) * mm, v(-10130.7, -2260.13) * mm, v(-10100.74, -2262.96) * mm, v(-10076.63, -2264.55) * mm, v(-10058.48, -2265.41) * mm, v(-10043.3, -2265.84) * mm, v(-10031.13, -2266.01) * mm, v(-10021.98, -2266.06) * mm, v(-10012.84, -2266.01) * mm, v(-10000.67, -2265.84) * mm, v(-9985.5, -2265.41) * mm, v(-9967.34, -2264.55) * mm, v(-9943.23, -2262.96) * mm, v(-9913.28, -2260.13) * mm, v(-9877.7, -2255.41) * mm, v(-9842.56, -2249.38) * mm, v(-9796.34, -2239.63) * mm, v(-9739.93, -2224.27) * mm, v(-9685.74, -2204.8) * mm, v(-9643.95, -2186.85) * mm, v(-9613.46, -2172.2) * mm, v(-9583.87, -2156.39) * mm, v(-9560.01, -2142.26) * mm, v(-9541.44, -2130.4) * mm, v(-9527.77, -2121.23) * mm, v(-9516.61, -2113.35) * mm, v(-9507.82, -2106.92) * mm, v(-9501.3, -2102.02) * mm, v(-9494.86, -2097.06) * mm, v(-9486.39, -2090.38) * mm, v(-9476.02, -2081.89) * mm, v(-9463.94, -2071.5) * mm, v(-9448.32, -2057.35) * mm, v(-9429.7, -2039.19) * mm, v(-9408.86, -2016.64) * mm, v(-9389.52, -1993.38) * mm, v(-9365.8, -1961.49) * mm, v(-9340.06, -1920.08) * mm, v(-9319.73, -1876.94) * mm, v(-9306.81, -1841.56) * mm, v(-9298.83, -1814.64) * mm, v(-9292.57, -1787.4) * mm, v(-9288.82, -1764.44) * mm, v(-9286.7, -1745.96) * mm, v(-9285.57, -1732.04) * mm, v(-9285, -1720.4) * mm, v(-9284.77, -1711.08) * mm, v(-9284.71, -1704.07) * mm, v(-9284.77, -1697.06) * mm, v(-9285, -1687.74) * mm, v(-9285.57, -1676.1) * mm, v(-9286.7, -1662.19) * mm, v(-9288.82, -1643.7) * mm, v(-9292.57, -1620.75) * mm, v(-9298.83, -1593.5) * mm, v(-9306.81, -1566.58) * mm, v(-9319.73, -1531.2) * mm, v(-9340.06, -1488.06) * mm, v(-9365.8, -1446.66) * mm, v(-9389.52, -1414.77) * mm, v(-9408.86, -1391.5) * mm, v(-9429.7, -1368.96) * mm, v(-9448.32, -1350.79) * mm, v(-9463.94, -1336.65) * mm, v(-9476.02, -1326.26) * mm, v(-9486.39, -1317.77) * mm, v(-9494.86, -1311.08) * mm, v(-9501.3, -1306.12) * mm, v(-9507.82, -1301.23) * mm, v(-9516.61, -1294.8) * mm, v(-9527.77, -1286.91) * mm, v(-9541.44, -1277.74) * mm, v(-9560.01, -1265.88) * mm, v(-9583.87, -1251.76) * mm, v(-9613.46, -1235.95) * mm, v(-9643.95, -1221.3) * mm, v(-9685.74, -1203.34) * mm, v(-9739.93, -1183.87) * mm, v(-9796.34, -1168.51) * mm, v(-9842.56, -1158.76) * mm, v(-9877.7, -1152.73) * mm, v(-9913.28, -1148.01) * mm, v(-9943.23, -1145.18) * mm, v(-9967.34, -1143.59) * mm, v(-9985.5, -1142.73) * mm, v(-10000.67, -1142.3) * mm, v(-10012.84, -1142.13) * mm, v(-10021.98, -1142.09) * mm, v(-10031.13, -1142.13) * mm, v(-10043.3, -1142.3) * mm, v(-10058.48, -1142.73) * mm, v(-10076.63, -1143.59) * mm, v(-10100.74, -1145.18) * mm, v(-10130.7, -1148.01) * mm, v(-10166.27, -1152.73) * mm, v(-10201.41, -1158.76) * mm, v(-10247.63, -1168.51) * mm, v(-10304.04, -1183.87) * mm, v(-10358.23, -1203.34) * mm, v(-10400.02, -1221.3) * mm, v(-10430.51, -1235.95) * mm, v(-10460.1, -1251.76) * mm, v(-10483.96, -1265.88) * mm, v(-10502.53, -1277.74) * mm, v(-10516.2, -1286.91) * mm, v(-10527.36, -1294.8) * mm, v(-10536.14, -1301.23) * mm, v(-10542.67, -1306.12) * mm, v(-10549.11, -1311.08) * mm, v(-10557.58, -1317.77) * mm, v(-10567.95, -1326.26) * mm, v(-10580.03, -1336.65) * mm, v(-10595.65, -1350.79) * mm, v(-10614.26, -1368.96) * mm, v(-10635.11, -1391.5) * mm, v(-10654.45, -1414.77) * mm, v(-10678.17, -1446.66) * mm, v(-10703.9, -1488.06) * mm, v(-10724.24, -1531.2) * mm, v(-10737.16, -1566.58) * mm, v(-10745.14, -1593.5) * mm, v(-10751.4, -1620.75) * mm, v(-10755.15, -1643.7) * mm, v(-10757.27, -1662.19) * mm, v(-10758.4, -1676.1) * mm, v(-10758.97, -1687.74) * mm, v(-10759.2, -1697.06) * mm, v(-10759.26, -1704.07) * mm, v(-10759.2, -1711.08) * mm], "construction": true});
            skArc(sketch, "E60", {"start": v(-9536.64, -1296.26) * mm, "mid": v(-9535.16, -1297.04) * mm, "end": v(-9533.69, -1297.83) * mm, "construction": true});
            skArc(sketch, "E61", {"start": v(-9536.64, -2111.88) * mm, "mid": v(-9535.16, -2111.1) * mm, "end": v(-9533.69, -2110.3) * mm, "construction": true});
            skArc(sketch, "E62", {"start": v(-9533.69, -1297.83) * mm, "mid": v(-9753.57, -1704.07) * mm, "end": v(-9533.69, -2110.3) * mm, "construction": true});
            skLineSegment(sketch, "E63", {"start": v(-9533.69, -1297.83) * mm, "end": v(-9533.69, -2110.3) * mm, "construction": true});
            skArc(sketch, "E64", {"start": v(-10432.44, -1571.33) * mm, "mid": v(-10211.18, -2095.74) * mm, "end": v(-9643.91, -2049.11) * mm, "construction": true});
            skLineSegment(sketch, "E65", {"start": v(-10432.44, -1571.33) * mm, "end": v(-9643.91, -2049.11) * mm, "construction": true});
            skLineSegment(sketch, "E66", {"start": v(-8702.7, -473.7) * mm, "end": v(-8702.7, 448.3) * mm});
            skArc(sketch, "E67", {"start": v(-8702.7, -473.7) * mm, "mid": v(-8368.86, -12.7) * mm, "end": v(-8702.7, 448.3) * mm});
            skPoint(sketch, "E68", {"position": v(-8702.7, -12.7) * mm});
            skSolve(sketch);
        }
        {
            var Q0;
            Q0=makeQuery(id+"F1.opExtrude","SWEPT_BODY",BODY,{"disambiguationData":[OSD([sQuery(id+"F0.wireOp",EDGE,"E4"),sQuery(id+"F0.wireOp",EDGE,"E6"),sQuery(id+"F0.wireOp",EDGE,"E7"),sQuery(id+"F0.wireOp",EDGE,"E8"),sQuery(id+"F0.wireOp",EDGE,"E9.0"),sQuery(id+"F0.wireOp",EDGE,"E9.1"),sQuery(id+"F0.wireOp",EDGE,"E11")])]});
            var Q1;
            Q1=sQuery(id+"F2.wireOp",EDGE,"E15");
            circularPattern(context, id + "F8", {"entities" : qUnion([Q0]), "axis" : qUnion([Q1]), "angle" : 360 * degree, "instanceCount" : 32, "equalSpace" : true});
        }
    });
